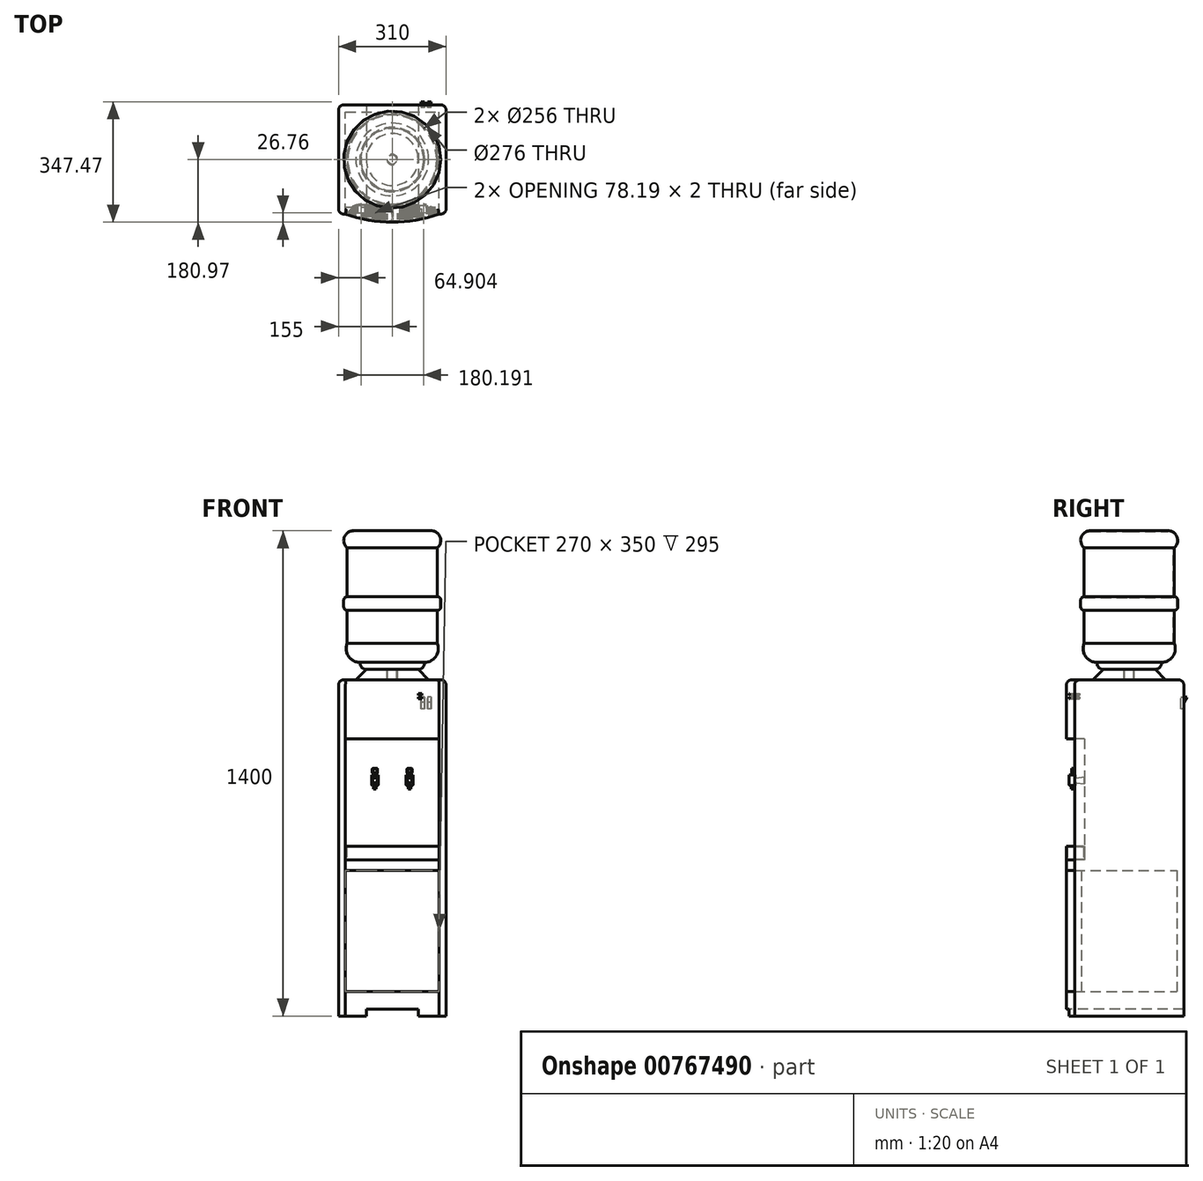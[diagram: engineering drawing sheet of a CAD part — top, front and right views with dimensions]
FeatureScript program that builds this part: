
annotation { "Feature Type Name" : "Feature", "Feature Type Description" : "" }
export const myFeature = defineFeature(function(context is Context, id is Id, definition is map)
    precondition{}
    {
        {
            var Q0;
            Q0=qCreatedBy(makeId("Top.planeOp"),FACE);
            var sketch = newSketch(context, id + "F0", { "sketchPlane" : qUnion([Q0])});
            skLineSegment(sketch, "E0.bottom", {"start": v(155, -157.5) * mm, "end": v(-155, -157.5) * mm});
            skLineSegment(sketch, "E0.top", {"start": v(155, 157.5) * mm, "end": v(-155, 157.5) * mm});
            skLineSegment(sketch, "E0.left", {"start": v(155, -157.5) * mm, "end": v(155, 157.5) * mm});
            skLineSegment(sketch, "E0.right", {"start": v(-155, -157.5) * mm, "end": v(-155, 157.5) * mm});
            skPoint(sketch, "E0.middle", {"position": v(0, 0) * mm});
            skArc(sketch, "E1", {"start": v(-135, -157.5) * mm, "mid": v(0, -180.97) * mm, "end": v(135, -157.5) * mm});
            skSolve(sketch);
        }
        {
            var Q0;
            Q0=makeQuery(id+"F0.imprint","IMPRINT",FACE,{"disambiguationData":[TD([[makeQuery(id+"F0.imprint","IMPRINT",EDGE,{"derivedFrom":sQuery(id+"F0.wireOp",EDGE,"E0.bottom")}),-1.0]])]});
            var Q1;
            {var subQ0=sQuery(id+"F0.wireOp",EDGE,"E1");Q1=makeQuery(id+"F0.imprint","IMPRINT",FACE,{"disambiguationData":[TD([[makeQuery(id+"F0.imprint","IMPRINT",EDGE,{"derivedFrom":subQ0}),1.0]])]});}
            extrude(context, id + "F1", {"entities" : qUnion([Q0, Q1]), "depth" : 970 * mm, "offsetDistance" : 25 * mm});
        }
        {
            var Q0;
            Q0=qCreatedBy(makeId("Front.planeOp"),FACE);
            var sketch = newSketch(context, id + "F2", { "sketchPlane" : qUnion([Q0])});
            skLineSegment(sketch, "E2.0", {"start": v(155, 970) * mm, "end": v(-155, 970) * mm});
            skLineSegment(sketch, "E3", {"start": v(105, 970) * mm, "end": v(75, 1000) * mm});
            skLineSegment(sketch, "E4", {"start": v(75, 1000) * mm, "end": v(0, 1000) * mm});
            skLineSegment(sketch, "E5", {"start": v(0, 1000) * mm, "end": v(0, 970) * mm});
            skLineSegment(sketch, "E6", {"start": v(15, 1000) * mm, "end": v(15, 970) * mm});
            skSolve(sketch);
        }
        {
            var Q0;
            {var subQ0=sQuery(id+"F2.wireOp",EDGE,"E3");Q0=makeQuery(id+"F2.imprint","IMPRINT",FACE,{"disambiguationData":[TD([[makeQuery(id+"F2.imprint","IMPRINT",EDGE,{"derivedFrom":subQ0}),1.0]])]});}
            var Q1;
            Q1=sQuery(id+"F2.wireOp",EDGE,"E5");
            revolve(context, id + "F3", {"operationType" : NewBodyOperationType.ADD, "surfaceOperationType" : NewSurfaceOperationType.NEW, "entities" : qUnion([Q0]), "axis" : qUnion([Q1]), "revolveType" : RevolveType.FULL});
        }
        {
            var Q0;
            Q0=qCreatedBy(makeId("Top.planeOp"),FACE);
            cPlane(context, id + "F4", {"entities" : qUnion([Q0]), "cplaneType" : CPlaneType.OFFSET, "offset" : 450 * mm, "width" : 150 * mm, "height" : 150 * mm});
        }
        {
            var Q0;
            Q0=qCreatedBy(id+"F4.planeOp",FACE);
            var sketch = newSketch(context, id + "F5", { "sketchPlane" : qUnion([Q0])});
            skArc(sketch, "E7.0.0", {"start": v(-135, -157.5) * mm, "mid": v(0, -180.97) * mm, "end": v(135, -157.5) * mm});
            skArc(sketch, "E7.0.2", {"start": v(135, -157.5) * mm, "mid": v(0, -180.97) * mm, "end": v(-135, -157.5) * mm});
            skLineSegment(sketch, "E8", {"start": v(-90, -129.3) * mm, "end": v(0, -129.3) * mm});
            skArc(sketch, "E9", {"start": v(-90, -129.3) * mm, "mid": v(-116.55, -136.93) * mm, "end": v(-135, -157.5) * mm});
            skLineSegment(sketch, "E10.MirrorCS", {"start": v(90, -129.3) * mm, "end": v(0, -129.3) * mm});
            skArc(sketch, "E11.MirrorCS", {"start": v(90, -129.3) * mm, "mid": v(116.55, -136.93) * mm, "end": v(135, -157.5) * mm});
            skSolve(sketch);
        }
        {
            var Q0;
            Q0=qSketchRegion(id+"F5",true);
            extrude(context, id + "F6", {"entities" : qUnion([Q0]), "operationType" : NewBodyOperationType.REMOVE, "depth" : 350 * mm, "offsetDistance" : 25 * mm});
        }
        {
            var Q0;
            Q0=qCreatedBy(makeId("Front.planeOp"),FACE);
            var sketch = newSketch(context, id + "F7", { "sketchPlane" : qUnion([Q0])});
            skLineSegment(sketch, "E12.0", {"start": v(-135, 450) * mm, "end": v(-135, 0) * mm});
            skLineSegment(sketch, "E12.1", {"start": v(135, 450) * mm, "end": v(135, 0) * mm});
            skLineSegment(sketch, "E13", {"start": v(-135, 420) * mm, "end": v(135, 420) * mm});
            skLineSegment(sketch, "E14", {"start": v(-135, 70) * mm, "end": v(135, 70) * mm});
            skSolve(sketch);
        }
        {
            var Q0;
            Q0=qSketchRegion(id+"F7",true);
            extrude(context, id + "F8", {"entities" : qUnion([Q0]), "operationType" : NewBodyOperationType.REMOVE, "endBound" : BoundingType.THROUGH_ALL, "depth" : 25 * mm, "offsetDistance" : 25 * mm, "hasSecondDirection" : true, "secondDirectionOppositeDirection" : true, "secondDirectionDepth" : (315 / 2 - 20) * mm});
        }
        {
            var Q0;
            Q0=qCreatedBy(makeId("Front.planeOp"),FACE);
            var sketch = newSketch(context, id + "F9", { "sketchPlane" : qUnion([Q0])});
            skLineSegment(sketch, "E15.bottom", {"start": v(-75, 20) * mm, "end": v(75, 20) * mm});
            skLineSegment(sketch, "E15.top", {"start": v(-75, 0) * mm, "end": v(75, 0) * mm});
            skLineSegment(sketch, "E15.left", {"start": v(-75, 20) * mm, "end": v(-75, 0) * mm});
            skLineSegment(sketch, "E15.right", {"start": v(75, 20) * mm, "end": v(75, 0) * mm});
            skSolve(sketch);
        }
        {
            var Q0;
            Q0=qSketchRegion(id+"F9",true);
            extrude(context, id + "F10", {"entities" : qUnion([Q0]), "operationType" : NewBodyOperationType.REMOVE, "endBound" : BoundingType.THROUGH_ALL, "oppositeDirection" : true, "depth" : 25 * mm, "offsetDistance" : 25 * mm, "hasSecondDirection" : true, "secondDirectionBound" : SecondDirectionBoundingType.THROUGH_ALL, "secondDirectionOppositeDirection" : false, "secondDirectionDepth" : 25 * mm});
        }
        {
            var Q0;
            Q0=qCreatedBy(makeId("Front.planeOp"),FACE);
            var sketch = newSketch(context, id + "F11", { "sketchPlane" : qUnion([Q0])});
            skLineSegment(sketch, "E16.0", {"start": v(-15, 1000) * mm, "end": v(15, 1000) * mm});
            skLineSegment(sketch, "E17.0.0", {"start": v(-15, 970) * mm, "end": v(15, 970) * mm});
            skLineSegment(sketch, "E18", {"start": v(-15, 970) * mm, "end": v(-15, 1000) * mm});
            skLineSegment(sketch, "E19", {"start": v(0, 1400) * mm, "end": v(-112, 1400) * mm});
            skLineSegment(sketch, "E20", {"start": v(-130, 1350.55) * mm, "end": v(-130, 1210) * mm});
            skLineSegment(sketch, "E21", {"start": v(-130, 1170) * mm, "end": v(-130, 1075) * mm});
            skLineSegment(sketch, "E22.0", {"start": v(-75, 1000) * mm, "end": v(75, 1000) * mm});
            skArc(sketch, "E23", {"start": v(-92.88, 1020.1) * mm, "mid": v(-88.45, 1006.04) * mm, "end": v(-75, 1000) * mm});
            skLineSegment(sketch, "E24", {"start": v(-140, 1200) * mm, "end": v(-140, 1180) * mm});
            skArc(sketch, "E25", {"start": v(-140, 1180) * mm, "mid": v(-137.07, 1172.93) * mm, "end": v(-130, 1170) * mm});
            skLineSegment(sketch, "E26", {"start": v(-140, 1180) * mm, "end": v(-130, 1180) * mm, "construction": true});
            skLineSegment(sketch, "E27", {"start": v(-130, 1170) * mm, "end": v(-130, 1180) * mm, "construction": true});
            skArc(sketch, "E28", {"start": v(-112, 1400) * mm, "mid": v(-138.31, 1381.58) * mm, "end": v(-130, 1350.55) * mm});
            skArc(sketch, "E29", {"start": v(-130, 1210) * mm, "mid": v(-137.07, 1207.07) * mm, "end": v(-140, 1200) * mm});
            skLineSegment(sketch, "E30", {"start": v(-140, 1200) * mm, "end": v(-130, 1200) * mm, "construction": true});
            skLineSegment(sketch, "E31", {"start": v(-130, 1210) * mm, "end": v(-130, 1200) * mm, "construction": true});
            skArc(sketch, "E32", {"start": v(-130, 1075) * mm, "mid": v(-126.01, 1037.7) * mm, "end": v(-92.88, 1020.1) * mm});
            skLineSegment(sketch, "E33", {"start": v(-92.88, 1020.1) * mm, "end": v(0, 1020.1) * mm});
            skLineSegment(sketch, "E34", {"start": v(0, 1400) * mm, "end": v(0, 970) * mm});
            skLineSegment(sketch, "E35.0", {"start": v(-75, 1002) * mm, "end": v(75, 1002) * mm});
            skArc(sketch, "E35.1", {"start": v(-90.44, 1022.18) * mm, "mid": v(-87.7, 1008.28) * mm, "end": v(-75, 1002) * mm});
            skArc(sketch, "E35.2", {"start": v(-128, 1074.6) * mm, "mid": v(-123.77, 1037.98) * mm, "end": v(-90.44, 1022.18) * mm});
            skLineSegment(sketch, "E35.3", {"start": v(-128, 1172.25) * mm, "end": v(-128, 1074.6) * mm});
            skArc(sketch, "E35.4", {"start": v(-138, 1180) * mm, "mid": v(-134.9, 1173.68) * mm, "end": v(-128, 1172.25) * mm});
            skLineSegment(sketch, "E35.5", {"start": v(-138, 1200) * mm, "end": v(-138, 1180) * mm});
            skLineSegment(sketch, "E35.6", {"start": v(0, 1398) * mm, "end": v(-112, 1398) * mm});
            skArc(sketch, "E35.7", {"start": v(-112, 1398) * mm, "mid": v(-136.58, 1380.46) * mm, "end": v(-128, 1351.5) * mm});
            skLineSegment(sketch, "E35.8", {"start": v(-128, 1351.5) * mm, "end": v(-128, 1207.75) * mm});
            skArc(sketch, "E35.9", {"start": v(-128, 1207.75) * mm, "mid": v(-134.9, 1206.32) * mm, "end": v(-138, 1200) * mm});
            skLineSegment(sketch, "E36", {"start": v(-13, 970) * mm, "end": v(-13, 1002) * mm});
            skSolve(sketch);
        }
        {
            var Q0;
            {var subQ3=sQuery(id+"F11.wireOp",EDGE,"E18");Q0=makeQuery(id+"F11.imprint","IMPRINT",FACE,{"disambiguationData":[TD([[makeQuery(id+"F11.imprint","IMPRINT",EDGE,{"derivedFrom":subQ3}),-1.0]])]});}
            var Q1;
            {var subQ0=sQuery(id+"F11.wireOp",EDGE,"E23");Q1=makeQuery(id+"F11.imprint","IMPRINT",FACE,{"disambiguationData":[TD([[makeQuery(id+"F11.imprint","IMPRINT",EDGE,{"derivedFrom":subQ0}),1.0]])]});}
            var Q2;
            {var subQ4=sQuery(id+"F11.wireOp",EDGE,"E19");Q2=makeQuery(id+"F11.imprint","IMPRINT",FACE,{"disambiguationData":[TD([[makeQuery(id+"F11.imprint","IMPRINT",EDGE,{"derivedFrom":subQ4}),1.0]])]});}
            var Q3;
            Q3=sQuery(id+"F11.wireOp",EDGE,"E34");
            revolve(context, id + "F12", {"surfaceOperationType" : NewSurfaceOperationType.NEW, "entities" : qUnion([Q0, Q1, Q2]), "axis" : qUnion([Q3]), "revolveType" : RevolveType.FULL});
        }
        {
            var Q0;
            Q0=makeQuery(id+"F1.opExtrude","SWEPT_EDGE",EDGE,{"disambiguationData":[OSD([sQuery(id+"F0.wireOp",EDGE,"E0.top"),sQuery(id+"F0.wireOp",EDGE,"E0.right")])]});
            var Q1;
            Q1=makeQuery(id+"F1.opExtrude","SWEPT_EDGE",EDGE,{"disambiguationData":[OSD([sQuery(id+"F0.wireOp",EDGE,"E0.bottom"),sQuery(id+"F0.wireOp",EDGE,"E0.right")])]});
            var Q2;
            Q2=makeQuery(id+"F1.opExtrude","SWEPT_EDGE",EDGE,{"disambiguationData":[OSD([sQuery(id+"F0.wireOp",EDGE,"E0.bottom"),sQuery(id+"F0.wireOp",EDGE,"E0.left")])]});
            var Q3;
            Q3=makeQuery(id+"F1.opExtrude","SWEPT_EDGE",EDGE,{"disambiguationData":[OSD([sQuery(id+"F0.wireOp",EDGE,"E0.top"),sQuery(id+"F0.wireOp",EDGE,"E0.left")])]});
            var Q4;
            Q4=makeQuery(id+"F1.opExtrude","CAP_EDGE",EDGE,{"disambiguationData":[OSD([sQuery(id+"F0.wireOp",EDGE,"E0.top")])],"isStart":false});
            var Q5;
            Q5=makeQuery(id+"F1.opExtrude","CAP_EDGE",EDGE,{"disambiguationData":[OSD([sQuery(id+"F0.wireOp",EDGE,"E0.left")])],"isStart":false});
            var Q6;
            Q6=makeQuery(id+"F1.opExtrude","CAP_EDGE",EDGE,{"disambiguationData":[OSD([sQuery(id+"F0.wireOp",EDGE,"E0.right")])],"isStart":false});
            var Q7;
            Q7=makeQuery(id+"F1.opExtrude","CAP_EDGE",EDGE,{"disambiguationData":[OSD([sQuery(id+"F0.wireOp",EDGE,"E1")])],"isStart":false});
            var Q8;
            {var subQ0=sQuery(id+"F0.wireOp",EDGE,"E0.bottom");Q8=makeQuery(id+"F1.opExtrude","CAP_EDGE",EDGE,{"disambiguationData":[OSD([subQ0]),TDD([makeQuery(id+"F0.imprint","IMPRINT",EDGE,{"disambiguationData":[TD([[makeQuery(id+"F0.imprint","INTERSECT",VERTEX,{"derivedFrom":[subQ0,sQuery(id+"F0.wireOp",EDGE,"E0.right")]}),1.0]])],"derivedFrom":subQ0})])],"isStart":false});}
            var Q9;
            {var subQ0=sQuery(id+"F0.wireOp",EDGE,"E0.bottom");Q9=makeQuery(id+"F1.opExtrude","CAP_EDGE",EDGE,{"disambiguationData":[OSD([subQ0]),TDD([makeQuery(id+"F0.imprint","IMPRINT",EDGE,{"disambiguationData":[TD([[makeQuery(id+"F0.imprint","INTERSECT",VERTEX,{"derivedFrom":[subQ0,sQuery(id+"F0.wireOp",EDGE,"E0.left")]}),-1.0]])],"derivedFrom":subQ0})])],"isStart":false});}
            fillet(context, id + "F13", {"entities" : qUnion([Q0, Q1, Q2, Q3, Q4, Q5, Q6, Q7, Q8, Q9]), "radius" : 15 * mm, "tangentPropagation" : true, "allowEdgeOverflow" : false});
        }
        {
            var Q0;
            Q0=makeQuery(id+"F6.boolean.opBoolean","COPY",FACE,{"derivedFrom":makeQuery(id+"F6.opExtrude","CAP_FACE",FACE,{"disambiguationData":[OSD([sQuery(id+"F5.wireOp",EDGE,"E7.0.2"),sQuery(id+"F5.wireOp",EDGE,"E8"),sQuery(id+"F5.wireOp",EDGE,"E9"),sQuery(id+"F5.wireOp",EDGE,"E10.MirrorCS"),sQuery(id+"F5.wireOp",EDGE,"E11.MirrorCS")])],"isStart":true})});
            var sketch = newSketch(context, id + "F14", { "sketchPlane" : qUnion([Q0])});
            skArc(sketch, "E37.0", {"start": v(-90, -129.3) * mm, "mid": v(-116.55, -136.93) * mm, "end": v(-135, -157.5) * mm});
            skLineSegment(sketch, "E37.1", {"start": v(90, -129.3) * mm, "end": v(-90, -129.3) * mm});
            skArc(sketch, "E37.2", {"start": v(90, -129.3) * mm, "mid": v(116.55, -136.93) * mm, "end": v(135, -157.5) * mm});
            skArc(sketch, "E37.3", {"start": v(135, -157.5) * mm, "mid": v(0, -180.97) * mm, "end": v(-135, -157.5) * mm});
            skSolve(sketch);
        }
        {
            var Q0;
            Q0=makeQuery(id+"F14.imprint","IMPRINT",FACE,{"disambiguationData":[TD([[makeQuery(id+"F14.imprint","IMPRINT",EDGE,{"derivedFrom":sQuery(id+"F14.wireOp",EDGE,"E37.0")}),1.0]])]});
            var Q1;
            Q1=qConstructionFilter(qBodyType(qCreatedBy(id+"F14",EDGE),BodyType.WIRE),ConstructionObject.NO);
            extrude(context, id + "F15", {"entities" : qUnion([Q0]), "surfaceEntities" : qUnion([Q1]), "depth" : 40 * mm, "offsetDistance" : 25 * mm});
        }
        {
            var Q0;
            Q0=makeQuery(id+"F15.opExtrude","CAP_FACE",FACE,{"disambiguationData":[OSD([sQuery(id+"F14.wireOp",EDGE,"E37.0"),sQuery(id+"F14.wireOp",EDGE,"E37.1"),sQuery(id+"F14.wireOp",EDGE,"E37.2"),sQuery(id+"F14.wireOp",EDGE,"E37.3")])],"isStart":false});
            shell(context, id + "F16", {"entities" : qUnion([Q0]), "thickness" : 2 * mm});
        }
        {
            var Q0;
            Q0=makeQuery(id+"F15.opExtrude","CAP_FACE",FACE,{"disambiguationData":[OSD([sQuery(id+"F14.wireOp",EDGE,"E37.0"),sQuery(id+"F14.wireOp",EDGE,"E37.1"),sQuery(id+"F14.wireOp",EDGE,"E37.2"),sQuery(id+"F14.wireOp",EDGE,"E37.3")])],"isStart":false});
            var sketch = newSketch(context, id + "F17", { "sketchPlane" : qUnion([Q0])});
            skArc(sketch, "E38.0", {"start": v(-90, -131.3) * mm, "mid": v(-114.54, -138.04) * mm, "end": v(-132.18, -156.38) * mm});
            skLineSegment(sketch, "E38.1", {"start": v(90, -131.3) * mm, "end": v(-90, -131.3) * mm});
            skArc(sketch, "E38.2", {"start": v(132.18, -156.38) * mm, "mid": v(0, -178.97) * mm, "end": v(-132.18, -156.38) * mm});
            skArc(sketch, "E38.3", {"start": v(90, -131.3) * mm, "mid": v(114.54, -138.04) * mm, "end": v(132.18, -156.38) * mm});
            skLineSegment(sketch, "E39.0", {"start": v(90, -133.3) * mm, "end": v(-90, -133.3) * mm});
            skArc(sketch, "E39.1", {"start": v(90, -133.3) * mm, "mid": v(112.5, -139.17) * mm, "end": v(129.24, -155.29) * mm});
            skArc(sketch, "E39.2", {"start": v(129.24, -155.29) * mm, "mid": v(0, -176.97) * mm, "end": v(-129.24, -155.29) * mm});
            skArc(sketch, "E39.3", {"start": v(-90, -133.3) * mm, "mid": v(-112.5, -139.17) * mm, "end": v(-129.24, -155.29) * mm});
            skLineSegment(sketch, "E40", {"start": v(0, -112.71) * mm, "end": v(0, -215.15) * mm, "construction": true});
            skLineSegment(sketch, "E41", {"start": v(-50, -106.6) * mm, "end": v(-50, -205.9) * mm, "construction": true});
            skLineSegment(sketch, "E42.bottom", {"start": v(-57.5, -156.3) * mm, "end": v(-42.5, -156.3) * mm});
            skLineSegment(sketch, "E42.top", {"start": v(-57.5, -171.3) * mm, "end": v(-42.5, -171.3) * mm});
            skLineSegment(sketch, "E42.left", {"start": v(-57.5, -156.3) * mm, "end": v(-57.5, -171.3) * mm});
            skLineSegment(sketch, "E42.right", {"start": v(-42.5, -156.3) * mm, "end": v(-42.5, -171.3) * mm});
            skLineSegment(sketch, "E43", {"start": v(-51, -156.3) * mm, "end": v(-51, -133.3) * mm});
            skLineSegment(sketch, "E44.MirrorCS", {"start": v(-49, -156.3) * mm, "end": v(-49, -133.3) * mm});
            skLineSegment(sketch, "E45", {"start": v(-51, -171.3) * mm, "end": v(-51, -173.67) * mm});
            skLineSegment(sketch, "E46", {"start": v(-49, -171.3) * mm, "end": v(-49, -173.93) * mm});
            skLineSegment(sketch, "E47", {"start": v(-1, -133.3) * mm, "end": v(-1, -176.97) * mm});
            skLineSegment(sketch, "E48", {"start": v(1, -133.3) * mm, "end": v(1, -176.97) * mm});
            skLineSegment(sketch, "E49", {"start": v(-49, -135.21) * mm, "end": v(-1, -135.21) * mm});
            skLineSegment(sketch, "E50.0.1.0", {"start": v(-49, -137.21) * mm, "end": v(-1, -137.21) * mm});
            skLineSegment(sketch, "E50.0.2.0", {"start": v(-49, -139.21) * mm, "end": v(-1, -139.21) * mm});
            skLineSegment(sketch, "E50.0.3.0", {"start": v(-49, -141.21) * mm, "end": v(-1, -141.21) * mm});
            skLineSegment(sketch, "E50.0.4.0", {"start": v(-49, -143.21) * mm, "end": v(-1, -143.21) * mm});
            skLineSegment(sketch, "E50.0.5.0", {"start": v(-49, -145.21) * mm, "end": v(-1, -145.21) * mm});
            skLineSegment(sketch, "E50.0.6.0", {"start": v(-49, -147.21) * mm, "end": v(-1, -147.21) * mm});
            skLineSegment(sketch, "E50.0.7.0", {"start": v(-49, -149.21) * mm, "end": v(-1, -149.21) * mm});
            skLineSegment(sketch, "E50.0.8.0", {"start": v(-49, -151.21) * mm, "end": v(-1, -151.21) * mm});
            skLineSegment(sketch, "E50.0.9.0", {"start": v(-49, -153.21) * mm, "end": v(-1, -153.21) * mm});
            skLineSegment(sketch, "E50.0.10.0", {"start": v(-49, -155.21) * mm, "end": v(-1, -155.21) * mm});
            skLineSegment(sketch, "E50.0.11.0", {"start": v(-42.5, -157.21) * mm, "end": v(-1, -157.21) * mm});
            skLineSegment(sketch, "E50.0.12.0", {"start": v(-44.5, -159.21) * mm, "end": v(-1, -159.21) * mm});
            skLineSegment(sketch, "E50.0.13.0", {"start": v(-44.5, -161.21) * mm, "end": v(-1, -161.21) * mm});
            skLineSegment(sketch, "E50.0.14.0", {"start": v(-44.5, -163.21) * mm, "end": v(-1, -163.21) * mm});
            skLineSegment(sketch, "E50.0.15.0", {"start": v(-49, -165.21) * mm, "end": v(-1, -165.21) * mm});
            skLineSegment(sketch, "E50.0.16.0", {"start": v(-49, -167.21) * mm, "end": v(-1, -167.21) * mm});
            skLineSegment(sketch, "E50.0.17.0", {"start": v(-49, -169.21) * mm, "end": v(-1, -169.21) * mm});
            skLineSegment(sketch, "E50.0.18.0", {"start": v(-49, -171.21) * mm, "end": v(-1, -171.21) * mm});
            skLineSegment(sketch, "E50.0.19.0", {"start": v(-49, -173.21) * mm, "end": v(-1, -173.21) * mm});
            skLineSegment(sketch, "E50.0.20.0", {"start": v(-49, -175.21) * mm, "end": v(-1, -175.21) * mm});
            skLineSegment(sketch, "E50.direction1", {"start": v(-49, -135.21) * mm, "end": v(-24, -135.21) * mm, "construction": true});
            skLineSegment(sketch, "E50.direction2", {"start": v(-49, -135.21) * mm, "end": v(-49, -137.21) * mm, "construction": true});
            skLineSegment(sketch, "E51.MirrorCS", {"start": v(-51, -137.21) * mm, "end": v(-108.57, -137.21) * mm});
            skLineSegment(sketch, "E52.MirrorCS", {"start": v(-51, -139.21) * mm, "end": v(-112.57, -139.21) * mm});
            skLineSegment(sketch, "E53.MirrorCS", {"start": v(-51, -141.21) * mm, "end": v(-115.8, -141.21) * mm});
            skLineSegment(sketch, "E54.MirrorCS", {"start": v(-51, -143.21) * mm, "end": v(-118.53, -143.21) * mm});
            skLineSegment(sketch, "E55.MirrorCS", {"start": v(-51, -145.21) * mm, "end": v(-120.9, -145.21) * mm});
            skLineSegment(sketch, "E56.MirrorCS", {"start": v(-51, -147.21) * mm, "end": v(-122.96, -147.21) * mm});
            skLineSegment(sketch, "E57.MirrorCS", {"start": v(-51, -149.21) * mm, "end": v(-124.8, -149.21) * mm});
            skLineSegment(sketch, "E58.MirrorCS", {"start": v(-51, -151.21) * mm, "end": v(-126.43, -151.21) * mm});
            skLineSegment(sketch, "E59.MirrorCS", {"start": v(-51, -153.21) * mm, "end": v(-127.89, -153.21) * mm});
            skLineSegment(sketch, "E60.MirrorCS", {"start": v(-51, -155.21) * mm, "end": v(-129.2, -155.21) * mm});
            skLineSegment(sketch, "E61.MirrorCS", {"start": v(-57.5, -157.21) * mm, "end": v(-123.53, -157.21) * mm});
            skLineSegment(sketch, "E62.MirrorCS", {"start": v(-57.5, -159.21) * mm, "end": v(-117.26, -159.21) * mm});
            skLineSegment(sketch, "E63.MirrorCS", {"start": v(-57.5, -161.21) * mm, "end": v(-110.6, -161.21) * mm});
            skLineSegment(sketch, "E64.MirrorCS", {"start": v(-57.5, -163.21) * mm, "end": v(-103.48, -163.21) * mm});
            skLineSegment(sketch, "E65.MirrorCS", {"start": v(-49, -165.21) * mm, "end": v(-50, -165.21) * mm});
            skLineSegment(sketch, "E66.MirrorCS", {"start": v(-57.5, -167.21) * mm, "end": v(-99, -167.21) * mm});
            skLineSegment(sketch, "E67.MirrorCS", {"start": v(-57.5, -169.21) * mm, "end": v(-99, -169.21) * mm});
            skLineSegment(sketch, "E68.MirrorCS", {"start": v(-51, -171.21) * mm, "end": v(-99, -171.21) * mm});
            skLineSegment(sketch, "E69.MirrorCS", {"start": v(-51, -173.21) * mm, "end": v(-99, -173.21) * mm});
            skPoint(sketch, "E70.orphan", {"position": v(-99, -137.21) * mm});
            skPoint(sketch, "E71.orphan", {"position": v(-99, -139.21) * mm});
            skPoint(sketch, "E72.orphan", {"position": v(-99, -141.21) * mm});
            skPoint(sketch, "E73.orphan", {"position": v(-99, -143.21) * mm});
            skPoint(sketch, "E74.orphan", {"position": v(-99, -145.21) * mm});
            skPoint(sketch, "E75.orphan", {"position": v(-99, -147.21) * mm});
            skPoint(sketch, "E76.orphan", {"position": v(-99, -149.21) * mm});
            skPoint(sketch, "E77.orphan", {"position": v(-99, -151.21) * mm});
            skPoint(sketch, "E78.orphan", {"position": v(-99, -153.21) * mm});
            skPoint(sketch, "E79.orphan", {"position": v(-99, -155.21) * mm});
            skPoint(sketch, "E80.orphan", {"position": v(-99, -157.21) * mm});
            skPoint(sketch, "E81.orphan", {"position": v(-99, -159.21) * mm});
            skPoint(sketch, "E82.orphan", {"position": v(-99, -161.21) * mm});
            skPoint(sketch, "E83.orphan", {"position": v(-99, -163.21) * mm});
            skLineSegment(sketch, "E84", {"start": v(-51, -135.21) * mm, "end": v(-103.14, -135.21) * mm});
            skLineSegment(sketch, "E85.0", {"start": v(-55.5, -158.3) * mm, "end": v(-44.5, -158.3) * mm});
            skLineSegment(sketch, "E85.1", {"start": v(-55.5, -158.3) * mm, "end": v(-55.5, -169.3) * mm});
            skLineSegment(sketch, "E85.2", {"start": v(-55.5, -169.3) * mm, "end": v(-44.5, -169.3) * mm});
            skLineSegment(sketch, "E85.3", {"start": v(-44.5, -158.3) * mm, "end": v(-44.5, -169.3) * mm});
            skPoint(sketch, "E86.orphan", {"position": v(-51, -157.21) * mm});
            skPoint(sketch, "E87.orphan", {"position": v(-51, -161.21) * mm});
            skPoint(sketch, "E88.orphan", {"position": v(-51, -165.21) * mm});
            skPoint(sketch, "E89.orphan", {"position": v(-51, -159.21) * mm});
            skPoint(sketch, "E90.orphan", {"position": v(-51, -163.21) * mm});
            skLineSegment(sketch, "E91.trimOffspring", {"start": v(-57.5, -165.21) * mm, "end": v(-99, -165.21) * mm});
            skPoint(sketch, "E92.orphan", {"position": v(-51, -167.21) * mm});
            skPoint(sketch, "E93.orphan", {"position": v(-51, -169.21) * mm});
            skPoint(sketch, "E94.orphan", {"position": v(-49, -159.21) * mm});
            skPoint(sketch, "E95.orphan", {"position": v(-49, -157.21) * mm});
            skPoint(sketch, "E96.orphan", {"position": v(-49, -161.21) * mm});
            skPoint(sketch, "E97.orphan", {"position": v(-49, -163.21) * mm});
            skLineSegment(sketch, "E98.MirrorCS", {"start": v(49, -165.21) * mm, "end": v(1, -165.21) * mm});
            skLineSegment(sketch, "E99.MirrorCS", {"start": v(44.5, -163.21) * mm, "end": v(1, -163.21) * mm});
            skLineSegment(sketch, "E100.MirrorCS", {"start": v(49, -167.21) * mm, "end": v(1, -167.21) * mm});
            skLineSegment(sketch, "E101.MirrorCS", {"start": v(44.5, -159.21) * mm, "end": v(1, -159.21) * mm});
            skLineSegment(sketch, "E102.MirrorCS", {"start": v(49, -171.21) * mm, "end": v(1, -171.21) * mm});
            skLineSegment(sketch, "E103.MirrorCS", {"start": v(42.5, -157.21) * mm, "end": v(1, -157.21) * mm});
            skLineSegment(sketch, "E104.MirrorCS", {"start": v(49, -175.21) * mm, "end": v(1, -175.21) * mm});
            skLineSegment(sketch, "E105.MirrorCS", {"start": v(49, -173.21) * mm, "end": v(1, -173.21) * mm});
            skLineSegment(sketch, "E106.MirrorCS", {"start": v(44.5, -161.21) * mm, "end": v(1, -161.21) * mm});
            skLineSegment(sketch, "E107.MirrorCS", {"start": v(49, -169.21) * mm, "end": v(1, -169.21) * mm});
            skLineSegment(sketch, "E108.MirrorCS", {"start": v(49, -135.21) * mm, "end": v(1, -135.21) * mm});
            skLineSegment(sketch, "E109.MirrorCS", {"start": v(49, -145.21) * mm, "end": v(1, -145.21) * mm});
            skLineSegment(sketch, "E110.MirrorCS", {"start": v(49, -137.21) * mm, "end": v(1, -137.21) * mm});
            skLineSegment(sketch, "E111.MirrorCS", {"start": v(49, -143.21) * mm, "end": v(1, -143.21) * mm});
            skLineSegment(sketch, "E112.MirrorCS", {"start": v(49, -153.21) * mm, "end": v(1, -153.21) * mm});
            skLineSegment(sketch, "E113.MirrorCS", {"start": v(49, -141.21) * mm, "end": v(1, -141.21) * mm});
            skLineSegment(sketch, "E114.MirrorCS", {"start": v(49, -151.21) * mm, "end": v(1, -151.21) * mm});
            skLineSegment(sketch, "E115.MirrorCS", {"start": v(49, -149.21) * mm, "end": v(1, -149.21) * mm});
            skLineSegment(sketch, "E116.MirrorCS", {"start": v(49, -147.21) * mm, "end": v(1, -147.21) * mm});
            skLineSegment(sketch, "E117.MirrorCS", {"start": v(49, -139.21) * mm, "end": v(1, -139.21) * mm});
            skLineSegment(sketch, "E118.MirrorCS", {"start": v(49, -155.21) * mm, "end": v(1, -155.21) * mm});
            skLineSegment(sketch, "E119.MirrorCS", {"start": v(42.5, -156.3) * mm, "end": v(42.5, -171.3) * mm});
            skLineSegment(sketch, "E120.MirrorCS", {"start": v(44.5, -158.3) * mm, "end": v(44.5, -169.3) * mm});
            skLineSegment(sketch, "E121.MirrorCS", {"start": v(55.5, -158.3) * mm, "end": v(55.5, -169.3) * mm});
            skLineSegment(sketch, "E122.MirrorCS", {"start": v(57.5, -156.3) * mm, "end": v(42.5, -156.3) * mm});
            skLineSegment(sketch, "E123.MirrorCS", {"start": v(51, -171.21) * mm, "end": v(99, -171.21) * mm});
            skLineSegment(sketch, "E124.MirrorCS", {"start": v(57.5, -156.3) * mm, "end": v(57.5, -171.3) * mm});
            skLineSegment(sketch, "E125.MirrorCS", {"start": v(57.5, -171.3) * mm, "end": v(42.5, -171.3) * mm});
            skLineSegment(sketch, "E126.MirrorCS", {"start": v(49, -171.3) * mm, "end": v(49, -173.93) * mm});
            skLineSegment(sketch, "E127.MirrorCS", {"start": v(51, -171.3) * mm, "end": v(51, -173.67) * mm});
            skLineSegment(sketch, "E128.MirrorCS", {"start": v(51, -151.21) * mm, "end": v(126.43, -151.21) * mm});
            skLineSegment(sketch, "E129.MirrorCS", {"start": v(51, -155.21) * mm, "end": v(129.2, -155.21) * mm});
            skLineSegment(sketch, "E130.MirrorCS", {"start": v(57.5, -165.21) * mm, "end": v(99, -165.21) * mm});
            skLineSegment(sketch, "E131.MirrorCS", {"start": v(57.5, -157.21) * mm, "end": v(123.53, -157.21) * mm});
            skLineSegment(sketch, "E132.MirrorCS", {"start": v(51, -153.21) * mm, "end": v(127.89, -153.21) * mm});
            skLineSegment(sketch, "E133.MirrorCS", {"start": v(57.5, -159.21) * mm, "end": v(117.26, -159.21) * mm});
            skLineSegment(sketch, "E134.MirrorCS", {"start": v(57.5, -167.21) * mm, "end": v(99, -167.21) * mm});
            skLineSegment(sketch, "E135.MirrorCS", {"start": v(51, -141.21) * mm, "end": v(115.8, -141.21) * mm});
            skLineSegment(sketch, "E136.MirrorCS", {"start": v(51, -149.21) * mm, "end": v(124.8, -149.21) * mm});
            skLineSegment(sketch, "E137.MirrorCS", {"start": v(51, -147.21) * mm, "end": v(122.96, -147.21) * mm});
            skLineSegment(sketch, "E138.MirrorCS", {"start": v(51, -137.21) * mm, "end": v(108.57, -137.21) * mm});
            skLineSegment(sketch, "E139.MirrorCS", {"start": v(57.5, -169.21) * mm, "end": v(99, -169.21) * mm});
            skLineSegment(sketch, "E140.MirrorCS", {"start": v(51, -145.21) * mm, "end": v(120.9, -145.21) * mm});
            skLineSegment(sketch, "E141.MirrorCS", {"start": v(51, -139.21) * mm, "end": v(112.57, -139.21) * mm});
            skLineSegment(sketch, "E142.MirrorCS", {"start": v(51, -135.21) * mm, "end": v(103.14, -135.21) * mm});
            skLineSegment(sketch, "E143.MirrorCS", {"start": v(-90, -133.3) * mm, "end": v(90, -133.3) * mm});
            skLineSegment(sketch, "E144.MirrorCS", {"start": v(51, -143.21) * mm, "end": v(118.53, -143.21) * mm});
            skLineSegment(sketch, "E145.MirrorCS", {"start": v(57.5, -163.21) * mm, "end": v(103.48, -163.21) * mm});
            skLineSegment(sketch, "E146.MirrorCS", {"start": v(57.5, -161.21) * mm, "end": v(110.6, -161.21) * mm});
            skPoint(sketch, "E147.MirrorP", {"position": v(99, -145.21) * mm});
            skPoint(sketch, "E148.MirrorP", {"position": v(99, -141.21) * mm});
            skPoint(sketch, "E149.MirrorP", {"position": v(99, -143.21) * mm});
            skPoint(sketch, "E150.MirrorP", {"position": v(99, -139.21) * mm});
            skPoint(sketch, "E151.MirrorP", {"position": v(99, -137.21) * mm});
            skPoint(sketch, "E152.MirrorP", {"position": v(99, -155.21) * mm});
            skPoint(sketch, "E153.MirrorP", {"position": v(99, -147.21) * mm});
            skPoint(sketch, "E154.MirrorP", {"position": v(99, -149.21) * mm});
            skPoint(sketch, "E155.MirrorP", {"position": v(99, -157.21) * mm});
            skPoint(sketch, "E156.MirrorP", {"position": v(99, -151.21) * mm});
            skPoint(sketch, "E157.MirrorP", {"position": v(99, -153.21) * mm});
            skLineSegment(sketch, "E158.MirrorCS", {"start": v(55.5, -158.3) * mm, "end": v(44.5, -158.3) * mm});
            skLineSegment(sketch, "E159.MirrorCS", {"start": v(55.5, -169.3) * mm, "end": v(44.5, -169.3) * mm});
            skLineSegment(sketch, "E160.MirrorCS", {"start": v(51, -156.3) * mm, "end": v(51, -133.3) * mm});
            skLineSegment(sketch, "E161.MirrorCS", {"start": v(49, -156.3) * mm, "end": v(49, -133.3) * mm});
            skLineSegment(sketch, "E162.MirrorCS", {"start": v(51, -173.21) * mm, "end": v(99, -173.21) * mm});
            skSolve(sketch);
        }
        {
            var Q0;
            {var subQ16=sQuery(id+"F17.wireOp",EDGE,"E38.0");Q0=makeQuery(id+"F17.imprint","IMPRINT",FACE,{"disambiguationData":[TD([[makeQuery(id+"F17.imprint","IMPRINT",EDGE,{"derivedFrom":subQ16}),1.0]])]});}
            var Q1;
            {var subQ0=sQuery(id+"F17.wireOp",EDGE,"E66.MirrorCS");var subQ1=sQuery(id+"F17.wireOp",EDGE,"E38.2");var subQ2=makeQuery(id+"F17.imprint","INTERSECT",VERTEX,{"derivedFrom":[subQ1,subQ0]});Q1=makeQuery(id+"F17.imprint","IMPRINT",FACE,{"disambiguationData":[TD([[makeQuery(id+"F17.imprint","IMPRINT",EDGE,{"disambiguationData":[TD([[subQ2,1.0]])],"derivedFrom":subQ1}),-1.0]])]});}
            var Q2;
            {var subQ0=sQuery(id+"F17.wireOp",EDGE,"E67.MirrorCS");var subQ1=sQuery(id+"F17.wireOp",EDGE,"E38.2");var subQ2=makeQuery(id+"F17.imprint","INTERSECT",VERTEX,{"derivedFrom":[subQ1,subQ0]});Q2=makeQuery(id+"F17.imprint","IMPRINT",FACE,{"disambiguationData":[TD([[makeQuery(id+"F17.imprint","IMPRINT",EDGE,{"disambiguationData":[TD([[subQ2,1.0]])],"derivedFrom":subQ1}),-1.0]])]});}
            var Q3;
            {var subQ0=sQuery(id+"F17.wireOp",EDGE,"E68.MirrorCS");var subQ1=sQuery(id+"F17.wireOp",EDGE,"E38.2");var subQ2=makeQuery(id+"F17.imprint","INTERSECT",VERTEX,{"derivedFrom":[subQ1,subQ0]});Q3=makeQuery(id+"F17.imprint","IMPRINT",FACE,{"disambiguationData":[TD([[makeQuery(id+"F17.imprint","IMPRINT",EDGE,{"disambiguationData":[TD([[subQ2,1.0]])],"derivedFrom":subQ1}),-1.0]])]});}
            var Q4;
            {var subQ0=sQuery(id+"F17.wireOp",EDGE,"E134.MirrorCS");var subQ1=sQuery(id+"F17.wireOp",EDGE,"E38.2");var subQ2=makeQuery(id+"F17.imprint","INTERSECT",VERTEX,{"derivedFrom":[subQ1,subQ0]});Q4=makeQuery(id+"F17.imprint","IMPRINT",FACE,{"disambiguationData":[TD([[makeQuery(id+"F17.imprint","IMPRINT",EDGE,{"disambiguationData":[TD([[subQ2,-1.0]])],"derivedFrom":subQ1}),-1.0]])]});}
            var Q5;
            {var subQ0=sQuery(id+"F17.wireOp",EDGE,"E123.MirrorCS");var subQ1=sQuery(id+"F17.wireOp",EDGE,"E38.2");var subQ2=makeQuery(id+"F17.imprint","INTERSECT",VERTEX,{"derivedFrom":[subQ1,subQ0]});Q5=makeQuery(id+"F17.imprint","IMPRINT",FACE,{"disambiguationData":[TD([[makeQuery(id+"F17.imprint","IMPRINT",EDGE,{"disambiguationData":[TD([[subQ2,1.0]])],"derivedFrom":subQ1}),-1.0]])]});}
            var Q6;
            {var subQ7=sQuery(id+"F17.wireOp",EDGE,"E69.MirrorCS");var subQ9=sQuery(id+"F17.wireOp",EDGE,"E38.2");var subQ10=makeQuery(id+"F17.imprint","INTERSECT",VERTEX,{"derivedFrom":[subQ9,subQ7]});Q6=makeQuery(id+"F17.imprint","IMPRINT",FACE,{"disambiguationData":[TD([[makeQuery(id+"F17.imprint","IMPRINT",EDGE,{"disambiguationData":[TD([[subQ10,1.0]])],"derivedFrom":subQ9}),-1.0]])]});}
            var Q7;
            {var subQ0=sQuery(id+"F17.wireOp",EDGE,"E162.MirrorCS");var subQ1=sQuery(id+"F17.wireOp",EDGE,"E38.2");var subQ2=makeQuery(id+"F17.imprint","INTERSECT",VERTEX,{"derivedFrom":[subQ1,subQ0]});Q7=makeQuery(id+"F17.imprint","IMPRINT",FACE,{"disambiguationData":[TD([[makeQuery(id+"F17.imprint","IMPRINT",EDGE,{"disambiguationData":[TD([[subQ2,1.0]])],"derivedFrom":subQ1}),-1.0]])]});}
            extrude(context, id + "F18", {"entities" : qUnion([Q0, Q1, Q2, Q3, Q4, Q5, Q6, Q7]), "oppositeDirection" : true, "depth" : 2 * mm, "offsetDistance" : 25 * mm});
        }
        {
            var Q0;
            {var subQ0=sQuery(id+"F17.wireOp",EDGE,"E47");var subQ7=sQuery(id+"F17.wireOp",EDGE,"E39.2");var subQ8=makeQuery(id+"F17.imprint","INTERSECT",VERTEX,{"derivedFrom":[subQ7,subQ0]});Q0=makeQuery(id+"F17.imprint","IMPRINT",FACE,{"disambiguationData":[TD([[makeQuery(id+"F17.imprint","IMPRINT",EDGE,{"disambiguationData":[TD([[subQ8,1.0]])],"derivedFrom":subQ7}),-1.0]])]});}
            var Q1;
            {var subQ0=sQuery(id+"F17.wireOp",EDGE,"E49");Q1=makeQuery(id+"F17.imprint","IMPRINT",FACE,{"disambiguationData":[TD([[makeQuery(id+"F17.imprint","IMPRINT",EDGE,{"derivedFrom":subQ0}),-1.0]])]});}
            var Q2;
            {var subQ0=sQuery(id+"F17.wireOp",EDGE,"E50.0.2.0");Q2=makeQuery(id+"F17.imprint","IMPRINT",FACE,{"disambiguationData":[TD([[makeQuery(id+"F17.imprint","IMPRINT",EDGE,{"derivedFrom":subQ0}),-1.0]])]});}
            var Q3;
            {var subQ0=sQuery(id+"F17.wireOp",EDGE,"E50.0.4.0");Q3=makeQuery(id+"F17.imprint","IMPRINT",FACE,{"disambiguationData":[TD([[makeQuery(id+"F17.imprint","IMPRINT",EDGE,{"derivedFrom":subQ0}),-1.0]])]});}
            var Q4;
            {var subQ0=sQuery(id+"F17.wireOp",EDGE,"E50.0.6.0");Q4=makeQuery(id+"F17.imprint","IMPRINT",FACE,{"disambiguationData":[TD([[makeQuery(id+"F17.imprint","IMPRINT",EDGE,{"derivedFrom":subQ0}),-1.0]])]});}
            var Q5;
            {var subQ0=sQuery(id+"F17.wireOp",EDGE,"E50.0.8.0");Q5=makeQuery(id+"F17.imprint","IMPRINT",FACE,{"disambiguationData":[TD([[makeQuery(id+"F17.imprint","IMPRINT",EDGE,{"derivedFrom":subQ0}),-1.0]])]});}
            var Q6;
            {var subQ0=sQuery(id+"F17.wireOp",EDGE,"E50.0.10.0");Q6=makeQuery(id+"F17.imprint","IMPRINT",FACE,{"disambiguationData":[TD([[makeQuery(id+"F17.imprint","IMPRINT",EDGE,{"derivedFrom":subQ0}),-1.0]])]});}
            var Q7;
            {var subQ0=sQuery(id+"F17.wireOp",EDGE,"E50.0.12.0");var subQ1=sQuery(id+"F17.wireOp",EDGE,"E42.right");var subQ2=makeQuery(id+"F17.imprint","INTERSECT",VERTEX,{"derivedFrom":[subQ1,subQ0]});Q7=makeQuery(id+"F17.imprint","IMPRINT",FACE,{"disambiguationData":[TD([[makeQuery(id+"F17.imprint","IMPRINT",EDGE,{"disambiguationData":[TD([[subQ2,-1.0]])],"derivedFrom":subQ1}),1.0]])]});}
            var Q8;
            {var subQ0=sQuery(id+"F17.wireOp",EDGE,"E50.0.14.0");var subQ1=sQuery(id+"F17.wireOp",EDGE,"E42.right");var subQ2=makeQuery(id+"F17.imprint","INTERSECT",VERTEX,{"derivedFrom":[subQ1,subQ0]});Q8=makeQuery(id+"F17.imprint","IMPRINT",FACE,{"disambiguationData":[TD([[makeQuery(id+"F17.imprint","IMPRINT",EDGE,{"disambiguationData":[TD([[subQ2,-1.0]])],"derivedFrom":subQ1}),1.0]])]});}
            var Q9;
            {var subQ0=sQuery(id+"F17.wireOp",EDGE,"E50.0.16.0");var subQ1=sQuery(id+"F17.wireOp",EDGE,"E42.right");var subQ2=makeQuery(id+"F17.imprint","INTERSECT",VERTEX,{"derivedFrom":[subQ1,subQ0]});Q9=makeQuery(id+"F17.imprint","IMPRINT",FACE,{"disambiguationData":[TD([[makeQuery(id+"F17.imprint","IMPRINT",EDGE,{"disambiguationData":[TD([[subQ2,-1.0]])],"derivedFrom":subQ1}),1.0]])]});}
            var Q10;
            {var subQ3=sQuery(id+"F17.wireOp",EDGE,"E50.0.19.0");Q10=makeQuery(id+"F17.imprint","IMPRINT",FACE,{"disambiguationData":[TD([[makeQuery(id+"F17.imprint","IMPRINT",EDGE,{"derivedFrom":subQ3}),1.0]])]});}
            var Q11;
            {var subQ0=sQuery(id+"F17.wireOp",EDGE,"E47");var subQ1=sQuery(id+"F17.wireOp",EDGE,"E39.2");var subQ2=makeQuery(id+"F17.imprint","INTERSECT",VERTEX,{"derivedFrom":[subQ1,subQ0]});Q11=makeQuery(id+"F17.imprint","IMPRINT",FACE,{"disambiguationData":[TD([[makeQuery(id+"F17.imprint","IMPRINT",EDGE,{"disambiguationData":[TD([[subQ2,-1.0]])],"derivedFrom":subQ1}),-1.0]])]});}
            var Q12;
            {var subQ17=sQuery(id+"F17.wireOp",EDGE,"E85.0");Q12=makeQuery(id+"F17.imprint","IMPRINT",FACE,{"disambiguationData":[TD([[makeQuery(id+"F17.imprint","IMPRINT",EDGE,{"derivedFrom":subQ17}),1.0]])]});}
            var Q13;
            {var subQ0=sQuery(id+"F17.wireOp",EDGE,"E50.0.12.0");var subQ1=sQuery(id+"F17.wireOp",EDGE,"E42.right");var subQ2=makeQuery(id+"F17.imprint","INTERSECT",VERTEX,{"derivedFrom":[subQ1,subQ0]});Q13=makeQuery(id+"F17.imprint","IMPRINT",FACE,{"disambiguationData":[TD([[makeQuery(id+"F17.imprint","IMPRINT",EDGE,{"disambiguationData":[TD([[subQ2,-1.0]])],"derivedFrom":subQ1}),-1.0]])]});}
            var Q14;
            {var subQ0=sQuery(id+"F17.wireOp",EDGE,"E50.0.13.0");var subQ1=sQuery(id+"F17.wireOp",EDGE,"E42.right");var subQ2=makeQuery(id+"F17.imprint","INTERSECT",VERTEX,{"derivedFrom":[subQ1,subQ0]});Q14=makeQuery(id+"F17.imprint","IMPRINT",FACE,{"disambiguationData":[TD([[makeQuery(id+"F17.imprint","IMPRINT",EDGE,{"disambiguationData":[TD([[subQ2,-1.0]])],"derivedFrom":subQ1}),-1.0]])]});}
            var Q15;
            {var subQ0=sQuery(id+"F17.wireOp",EDGE,"E50.0.14.0");var subQ1=sQuery(id+"F17.wireOp",EDGE,"E42.right");var subQ2=makeQuery(id+"F17.imprint","INTERSECT",VERTEX,{"derivedFrom":[subQ1,subQ0]});Q15=makeQuery(id+"F17.imprint","IMPRINT",FACE,{"disambiguationData":[TD([[makeQuery(id+"F17.imprint","IMPRINT",EDGE,{"disambiguationData":[TD([[subQ2,-1.0]])],"derivedFrom":subQ1}),-1.0]])]});}
            var Q16;
            {var subQ0=sQuery(id+"F17.wireOp",EDGE,"E50.0.15.0");var subQ1=sQuery(id+"F17.wireOp",EDGE,"E42.right");var subQ2=makeQuery(id+"F17.imprint","INTERSECT",VERTEX,{"derivedFrom":[subQ1,subQ0]});Q16=makeQuery(id+"F17.imprint","IMPRINT",FACE,{"disambiguationData":[TD([[makeQuery(id+"F17.imprint","IMPRINT",EDGE,{"disambiguationData":[TD([[subQ2,-1.0]])],"derivedFrom":subQ1}),-1.0]])]});}
            var Q17;
            {var subQ0=sQuery(id+"F17.wireOp",EDGE,"E50.0.16.0");var subQ1=sQuery(id+"F17.wireOp",EDGE,"E42.right");var subQ2=makeQuery(id+"F17.imprint","INTERSECT",VERTEX,{"derivedFrom":[subQ1,subQ0]});Q17=makeQuery(id+"F17.imprint","IMPRINT",FACE,{"disambiguationData":[TD([[makeQuery(id+"F17.imprint","IMPRINT",EDGE,{"disambiguationData":[TD([[subQ2,-1.0]])],"derivedFrom":subQ1}),-1.0]])]});}
            var Q18;
            {var subQ10=sQuery(id+"F17.wireOp",EDGE,"E42.bottom");var subQ13=sQuery(id+"F17.wireOp",EDGE,"E43");var subQ21=makeQuery(id+"F17.imprint","INTERSECT",VERTEX,{"derivedFrom":[subQ10,subQ13]});Q18=makeQuery(id+"F17.imprint","IMPRINT",FACE,{"disambiguationData":[TD([[makeQuery(id+"F17.imprint","IMPRINT",EDGE,{"disambiguationData":[TD([[subQ21,-1.0]])],"derivedFrom":subQ10}),1.0]])]});}
            var Q19;
            {var subQ0=sQuery(id+"F17.wireOp",EDGE,"E45");var subQ6=sQuery(id+"F17.wireOp",EDGE,"E39.2");var subQ7=makeQuery(id+"F17.imprint","INTERSECT",VERTEX,{"derivedFrom":[subQ6,subQ0]});Q19=makeQuery(id+"F17.imprint","IMPRINT",FACE,{"disambiguationData":[TD([[makeQuery(id+"F17.imprint","IMPRINT",EDGE,{"disambiguationData":[TD([[subQ7,1.0]])],"derivedFrom":subQ6}),-1.0]])]});}
            var Q20;
            {var subQ3=sQuery(id+"F17.wireOp",EDGE,"E69.MirrorCS");var subQ9=sQuery(id+"F17.wireOp",EDGE,"E39.2");var subQ10=makeQuery(id+"F17.imprint","INTERSECT",VERTEX,{"derivedFrom":[subQ9,subQ3]});Q20=makeQuery(id+"F17.imprint","IMPRINT",FACE,{"disambiguationData":[TD([[makeQuery(id+"F17.imprint","IMPRINT",EDGE,{"disambiguationData":[TD([[subQ10,-1.0]])],"derivedFrom":subQ9}),-1.0]])]});}
            var Q21;
            {var subQ0=sQuery(id+"F17.wireOp",EDGE,"E67.MirrorCS");var subQ1=sQuery(id+"F17.wireOp",EDGE,"E39.2");var subQ2=makeQuery(id+"F17.imprint","INTERSECT",VERTEX,{"derivedFrom":[subQ1,subQ0]});Q21=makeQuery(id+"F17.imprint","IMPRINT",FACE,{"disambiguationData":[TD([[makeQuery(id+"F17.imprint","IMPRINT",EDGE,{"disambiguationData":[TD([[subQ2,-1.0]])],"derivedFrom":subQ1}),-1.0]])]});}
            var Q22;
            {var subQ0=sQuery(id+"F17.wireOp",EDGE,"E64.MirrorCS");Q22=makeQuery(id+"F17.imprint","IMPRINT",FACE,{"disambiguationData":[TD([[makeQuery(id+"F17.imprint","IMPRINT",EDGE,{"derivedFrom":subQ0}),1.0]])]});}
            var Q23;
            {var subQ0=sQuery(id+"F17.wireOp",EDGE,"E62.MirrorCS");Q23=makeQuery(id+"F17.imprint","IMPRINT",FACE,{"disambiguationData":[TD([[makeQuery(id+"F17.imprint","IMPRINT",EDGE,{"derivedFrom":subQ0}),1.0]])]});}
            var Q24;
            {var subQ6=sQuery(id+"F17.wireOp",EDGE,"E60.MirrorCS");Q24=makeQuery(id+"F17.imprint","IMPRINT",FACE,{"disambiguationData":[TD([[makeQuery(id+"F17.imprint","IMPRINT",EDGE,{"derivedFrom":subQ6}),1.0]])]});}
            var Q25;
            {var subQ0=sQuery(id+"F17.wireOp",EDGE,"E58.MirrorCS");Q25=makeQuery(id+"F17.imprint","IMPRINT",FACE,{"disambiguationData":[TD([[makeQuery(id+"F17.imprint","IMPRINT",EDGE,{"derivedFrom":subQ0}),1.0]])]});}
            var Q26;
            {var subQ0=sQuery(id+"F17.wireOp",EDGE,"E56.MirrorCS");Q26=makeQuery(id+"F17.imprint","IMPRINT",FACE,{"disambiguationData":[TD([[makeQuery(id+"F17.imprint","IMPRINT",EDGE,{"derivedFrom":subQ0}),1.0]])]});}
            var Q27;
            {var subQ0=sQuery(id+"F17.wireOp",EDGE,"E54.MirrorCS");Q27=makeQuery(id+"F17.imprint","IMPRINT",FACE,{"disambiguationData":[TD([[makeQuery(id+"F17.imprint","IMPRINT",EDGE,{"derivedFrom":subQ0}),1.0]])]});}
            var Q28;
            {var subQ0=sQuery(id+"F17.wireOp",EDGE,"E52.MirrorCS");Q28=makeQuery(id+"F17.imprint","IMPRINT",FACE,{"disambiguationData":[TD([[makeQuery(id+"F17.imprint","IMPRINT",EDGE,{"derivedFrom":subQ0}),1.0]])]});}
            var Q29;
            {var subQ0=sQuery(id+"F17.wireOp",EDGE,"E51.MirrorCS");Q29=makeQuery(id+"F17.imprint","IMPRINT",FACE,{"disambiguationData":[TD([[makeQuery(id+"F17.imprint","IMPRINT",EDGE,{"derivedFrom":subQ0}),-1.0]])]});}
            var Q30;
            {var subQ0=sQuery(id+"F17.wireOp",EDGE,"E108.MirrorCS");Q30=makeQuery(id+"F17.imprint","IMPRINT",FACE,{"disambiguationData":[TD([[makeQuery(id+"F17.imprint","IMPRINT",EDGE,{"derivedFrom":subQ0}),1.0]])]});}
            var Q31;
            {var subQ0=sQuery(id+"F17.wireOp",EDGE,"E113.MirrorCS");Q31=makeQuery(id+"F17.imprint","IMPRINT",FACE,{"disambiguationData":[TD([[makeQuery(id+"F17.imprint","IMPRINT",EDGE,{"derivedFrom":subQ0}),-1.0]])]});}
            var Q32;
            {var subQ0=sQuery(id+"F17.wireOp",EDGE,"E109.MirrorCS");Q32=makeQuery(id+"F17.imprint","IMPRINT",FACE,{"disambiguationData":[TD([[makeQuery(id+"F17.imprint","IMPRINT",EDGE,{"derivedFrom":subQ0}),-1.0]])]});}
            var Q33;
            {var subQ0=sQuery(id+"F17.wireOp",EDGE,"E115.MirrorCS");Q33=makeQuery(id+"F17.imprint","IMPRINT",FACE,{"disambiguationData":[TD([[makeQuery(id+"F17.imprint","IMPRINT",EDGE,{"derivedFrom":subQ0}),-1.0]])]});}
            var Q34;
            {var subQ0=sQuery(id+"F17.wireOp",EDGE,"E112.MirrorCS");Q34=makeQuery(id+"F17.imprint","IMPRINT",FACE,{"disambiguationData":[TD([[makeQuery(id+"F17.imprint","IMPRINT",EDGE,{"derivedFrom":subQ0}),-1.0]])]});}
            var Q35;
            {var subQ1=sQuery(id+"F17.wireOp",EDGE,"E103.MirrorCS");Q35=makeQuery(id+"F17.imprint","IMPRINT",FACE,{"disambiguationData":[TD([[makeQuery(id+"F17.imprint","IMPRINT",EDGE,{"derivedFrom":subQ1}),-1.0]])]});}
            var Q36;
            {var subQ0=sQuery(id+"F17.wireOp",EDGE,"E101.MirrorCS");var subQ1=sQuery(id+"F17.wireOp",EDGE,"E48");var subQ2=makeQuery(id+"F17.imprint","INTERSECT",VERTEX,{"derivedFrom":[subQ1,subQ0]});Q36=makeQuery(id+"F17.imprint","IMPRINT",FACE,{"disambiguationData":[TD([[makeQuery(id+"F17.imprint","IMPRINT",EDGE,{"disambiguationData":[TD([[subQ2,-1.0]])],"derivedFrom":subQ1}),1.0]])]});}
            var Q37;
            {var subQ0=sQuery(id+"F17.wireOp",EDGE,"E98.MirrorCS");var subQ1=sQuery(id+"F17.wireOp",EDGE,"E48");var subQ2=makeQuery(id+"F17.imprint","INTERSECT",VERTEX,{"derivedFrom":[subQ1,subQ0]});Q37=makeQuery(id+"F17.imprint","IMPRINT",FACE,{"disambiguationData":[TD([[makeQuery(id+"F17.imprint","IMPRINT",EDGE,{"disambiguationData":[TD([[subQ2,1.0]])],"derivedFrom":subQ1}),1.0]])]});}
            var Q38;
            {var subQ0=sQuery(id+"F17.wireOp",EDGE,"E100.MirrorCS");var subQ1=sQuery(id+"F17.wireOp",EDGE,"E48");var subQ2=makeQuery(id+"F17.imprint","INTERSECT",VERTEX,{"derivedFrom":[subQ1,subQ0]});Q38=makeQuery(id+"F17.imprint","IMPRINT",FACE,{"disambiguationData":[TD([[makeQuery(id+"F17.imprint","IMPRINT",EDGE,{"disambiguationData":[TD([[subQ2,-1.0]])],"derivedFrom":subQ1}),1.0]])]});}
            var Q39;
            {var subQ5=sQuery(id+"F17.wireOp",EDGE,"E105.MirrorCS");Q39=makeQuery(id+"F17.imprint","IMPRINT",FACE,{"disambiguationData":[TD([[makeQuery(id+"F17.imprint","IMPRINT",EDGE,{"derivedFrom":subQ5}),-1.0]])]});}
            var Q40;
            {var subQ0=sQuery(id+"F17.wireOp",EDGE,"E48");var subQ1=sQuery(id+"F17.wireOp",EDGE,"E39.2");var subQ2=makeQuery(id+"F17.imprint","INTERSECT",VERTEX,{"derivedFrom":[subQ1,subQ0]});Q40=makeQuery(id+"F17.imprint","IMPRINT",FACE,{"disambiguationData":[TD([[makeQuery(id+"F17.imprint","IMPRINT",EDGE,{"disambiguationData":[TD([[subQ2,1.0]])],"derivedFrom":subQ1}),-1.0]])]});}
            var Q41;
            {var subQ0=sQuery(id+"F17.wireOp",EDGE,"E120.MirrorCS");var subQ1=sQuery(id+"F17.wireOp",EDGE,"E98.MirrorCS");var subQ2=makeQuery(id+"F17.imprint","INTERSECT",VERTEX,{"derivedFrom":[subQ1,subQ0]});Q41=makeQuery(id+"F17.imprint","IMPRINT",FACE,{"disambiguationData":[TD([[makeQuery(id+"F17.imprint","IMPRINT",EDGE,{"disambiguationData":[TD([[subQ2,-1.0]])],"derivedFrom":subQ1}),1.0]])]});}
            var Q42;
            {var subQ0=sQuery(id+"F17.wireOp",EDGE,"E120.MirrorCS");var subQ1=sQuery(id+"F17.wireOp",EDGE,"E100.MirrorCS");var subQ2=makeQuery(id+"F17.imprint","INTERSECT",VERTEX,{"derivedFrom":[subQ1,subQ0]});Q42=makeQuery(id+"F17.imprint","IMPRINT",FACE,{"disambiguationData":[TD([[makeQuery(id+"F17.imprint","IMPRINT",EDGE,{"disambiguationData":[TD([[subQ2,-1.0]])],"derivedFrom":subQ1}),1.0]])]});}
            var Q43;
            Q43=makeQuery(id+"F17.imprint","IMPRINT",FACE,{"disambiguationData":[TD([[makeQuery(id+"F17.imprint","IMPRINT",EDGE,{"derivedFrom":sQuery(id+"F17.wireOp",EDGE,"E121.MirrorCS")}),1.0]])]});
            var Q44;
            {var subQ0=sQuery(id+"F17.wireOp",EDGE,"E120.MirrorCS");var subQ1=sQuery(id+"F17.wireOp",EDGE,"E98.MirrorCS");var subQ2=makeQuery(id+"F17.imprint","INTERSECT",VERTEX,{"derivedFrom":[subQ1,subQ0]});Q44=makeQuery(id+"F17.imprint","IMPRINT",FACE,{"disambiguationData":[TD([[makeQuery(id+"F17.imprint","IMPRINT",EDGE,{"disambiguationData":[TD([[subQ2,-1.0]])],"derivedFrom":subQ1}),-1.0]])]});}
            var Q45;
            {var subQ0=sQuery(id+"F17.wireOp",EDGE,"E120.MirrorCS");var subQ1=sQuery(id+"F17.wireOp",EDGE,"E99.MirrorCS");var subQ2=makeQuery(id+"F17.imprint","INTERSECT",VERTEX,{"derivedFrom":[subQ1,subQ0]});Q45=makeQuery(id+"F17.imprint","IMPRINT",FACE,{"disambiguationData":[TD([[makeQuery(id+"F17.imprint","IMPRINT",EDGE,{"disambiguationData":[TD([[subQ2,-1.0]])],"derivedFrom":subQ1}),-1.0]])]});}
            var Q46;
            {var subQ0=sQuery(id+"F17.wireOp",EDGE,"E120.MirrorCS");var subQ1=sQuery(id+"F17.wireOp",EDGE,"E101.MirrorCS");var subQ2=makeQuery(id+"F17.imprint","INTERSECT",VERTEX,{"derivedFrom":[subQ1,subQ0]});Q46=makeQuery(id+"F17.imprint","IMPRINT",FACE,{"disambiguationData":[TD([[makeQuery(id+"F17.imprint","IMPRINT",EDGE,{"disambiguationData":[TD([[subQ2,-1.0]])],"derivedFrom":subQ1}),1.0]])]});}
            var Q47;
            {var subQ6=sQuery(id+"F17.wireOp",EDGE,"E127.MirrorCS");Q47=makeQuery(id+"F17.imprint","IMPRINT",FACE,{"disambiguationData":[TD([[makeQuery(id+"F17.imprint","IMPRINT",EDGE,{"derivedFrom":subQ6}),-1.0]])]});}
            var Q48;
            {var subQ8=sQuery(id+"F17.wireOp",EDGE,"E122.MirrorCS");var subQ10=sQuery(id+"F17.wireOp",EDGE,"E160.MirrorCS");var subQ21=makeQuery(id+"F17.imprint","INTERSECT",VERTEX,{"derivedFrom":[subQ8,subQ10]});Q48=makeQuery(id+"F17.imprint","IMPRINT",FACE,{"disambiguationData":[TD([[makeQuery(id+"F17.imprint","IMPRINT",EDGE,{"disambiguationData":[TD([[subQ21,-1.0]])],"derivedFrom":subQ8}),-1.0]])]});}
            var Q49;
            {var subQ0=sQuery(id+"F17.wireOp",EDGE,"E142.MirrorCS");Q49=makeQuery(id+"F17.imprint","IMPRINT",FACE,{"disambiguationData":[TD([[makeQuery(id+"F17.imprint","IMPRINT",EDGE,{"derivedFrom":subQ0}),-1.0]])]});}
            var Q50;
            {var subQ0=sQuery(id+"F17.wireOp",EDGE,"E141.MirrorCS");Q50=makeQuery(id+"F17.imprint","IMPRINT",FACE,{"disambiguationData":[TD([[makeQuery(id+"F17.imprint","IMPRINT",EDGE,{"derivedFrom":subQ0}),-1.0]])]});}
            var Q51;
            {var subQ0=sQuery(id+"F17.wireOp",EDGE,"E140.MirrorCS");Q51=makeQuery(id+"F17.imprint","IMPRINT",FACE,{"disambiguationData":[TD([[makeQuery(id+"F17.imprint","IMPRINT",EDGE,{"derivedFrom":subQ0}),1.0]])]});}
            var Q52;
            {var subQ0=sQuery(id+"F17.wireOp",EDGE,"E137.MirrorCS");Q52=makeQuery(id+"F17.imprint","IMPRINT",FACE,{"disambiguationData":[TD([[makeQuery(id+"F17.imprint","IMPRINT",EDGE,{"derivedFrom":subQ0}),-1.0]])]});}
            var Q53;
            {var subQ0=sQuery(id+"F17.wireOp",EDGE,"E128.MirrorCS");Q53=makeQuery(id+"F17.imprint","IMPRINT",FACE,{"disambiguationData":[TD([[makeQuery(id+"F17.imprint","IMPRINT",EDGE,{"derivedFrom":subQ0}),-1.0]])]});}
            var Q54;
            {var subQ3=sQuery(id+"F17.wireOp",EDGE,"E131.MirrorCS");Q54=makeQuery(id+"F17.imprint","IMPRINT",FACE,{"disambiguationData":[TD([[makeQuery(id+"F17.imprint","IMPRINT",EDGE,{"derivedFrom":subQ3}),1.0]])]});}
            var Q55;
            {var subQ0=sQuery(id+"F17.wireOp",EDGE,"E133.MirrorCS");Q55=makeQuery(id+"F17.imprint","IMPRINT",FACE,{"disambiguationData":[TD([[makeQuery(id+"F17.imprint","IMPRINT",EDGE,{"derivedFrom":subQ0}),-1.0]])]});}
            var Q56;
            {var subQ0=sQuery(id+"F17.wireOp",EDGE,"E145.MirrorCS");Q56=makeQuery(id+"F17.imprint","IMPRINT",FACE,{"disambiguationData":[TD([[makeQuery(id+"F17.imprint","IMPRINT",EDGE,{"derivedFrom":subQ0}),-1.0]])]});}
            var Q57;
            {var subQ0=sQuery(id+"F17.wireOp",EDGE,"E134.MirrorCS");var subQ1=sQuery(id+"F17.wireOp",EDGE,"E39.2");var subQ2=makeQuery(id+"F17.imprint","INTERSECT",VERTEX,{"derivedFrom":[subQ1,subQ0]});Q57=makeQuery(id+"F17.imprint","IMPRINT",FACE,{"disambiguationData":[TD([[makeQuery(id+"F17.imprint","IMPRINT",EDGE,{"disambiguationData":[TD([[subQ2,-1.0]])],"derivedFrom":subQ1}),-1.0]])]});}
            var Q58;
            {var subQ3=sQuery(id+"F17.wireOp",EDGE,"E123.MirrorCS");var subQ5=sQuery(id+"F17.wireOp",EDGE,"E39.2");var subQ6=makeQuery(id+"F17.imprint","INTERSECT",VERTEX,{"derivedFrom":[subQ5,subQ3]});Q58=makeQuery(id+"F17.imprint","IMPRINT",FACE,{"disambiguationData":[TD([[makeQuery(id+"F17.imprint","IMPRINT",EDGE,{"disambiguationData":[TD([[subQ6,-1.0]])],"derivedFrom":subQ5}),-1.0]])]});}
            extrude(context, id + "F19", {"entities" : qUnion([Q0, Q1, Q2, Q3, Q4, Q5, Q6, Q7, Q8, Q9, Q10, Q11, Q12, Q13, Q14, Q15, Q16, Q17, Q18, Q19, Q20, Q21, Q22, Q23, Q24, Q25, Q26, Q27, Q28, Q29, Q30, Q31, Q32, Q33, Q34, Q35, Q36, Q37, Q38, Q39, Q40, Q41, Q42, Q43, Q44, Q45, Q46, Q47, Q48, Q49, Q50, Q51, Q52, Q53, Q54, Q55, Q56, Q57, Q58]), "operationType" : NewBodyOperationType.ADD, "oppositeDirection" : true, "depth" : 2 * mm, "offsetDistance" : 25 * mm});
        }
        {
            var Q0;
            Q0=makeQuery(id+"F8.boolean.opBoolean","COPY",FACE,{"derivedFrom":makeQuery(id+"F8.opExtrude","SWEPT_FACE",FACE,{"disambiguationData":[OSD([sQuery(id+"F7.wireOp",EDGE,"E14")])]})});
            var sketch = newSketch(context, id + "F20", { "sketchPlane" : qUnion([Q0])});
            skArc(sketch, "E163.0", {"start": v(-135, -157.5) * mm, "mid": v(0, -180.97) * mm, "end": v(135, -157.5) * mm});
            skLineSegment(sketch, "E164", {"start": v(-135, -157.5) * mm, "end": v(-135, -137.5) * mm});
            skLineSegment(sketch, "E165", {"start": v(-135, -137.5) * mm, "end": v(135, -137.5) * mm});
            skLineSegment(sketch, "E166", {"start": v(135, -137.5) * mm, "end": v(135, -157.5) * mm});
            skSolve(sketch);
        }
        {
            var Q0;
            Q0=qSketchRegion(id+"F20",true);
            var Q1;
            Q1=makeQuery(id+"F8.boolean.opBoolean","COPY",FACE,{"derivedFrom":makeQuery(id+"F8.opExtrude","SWEPT_FACE",FACE,{"disambiguationData":[OSD([sQuery(id+"F7.wireOp",EDGE,"E13")])]})});
            extrude(context, id + "F21", {"entities" : qUnion([Q0]), "endBound" : BoundingType.UP_TO_SURFACE, "depth" : 25 * mm, "endBoundEntityFace" : qUnion([Q1]), "offsetDistance" : 25 * mm});
        }
        {
            var Q0;
            Q0=makeQuery(id+"F6.boolean.opBoolean","COPY",FACE,{"derivedFrom":makeQuery(id+"F6.opExtrude","CAP_FACE",FACE,{"disambiguationData":[OSD([sQuery(id+"F5.wireOp",EDGE,"E7.0.2"),sQuery(id+"F5.wireOp",EDGE,"E8"),sQuery(id+"F5.wireOp",EDGE,"E9"),sQuery(id+"F5.wireOp",EDGE,"E10.MirrorCS"),sQuery(id+"F5.wireOp",EDGE,"E11.MirrorCS")])],"isStart":true})});
            cPlane(context, id + "F22", {"entities" : qUnion([Q0]), "cplaneType" : CPlaneType.OFFSET, "offset" : 230 * mm, "width" : 150 * mm, "height" : 150 * mm});
        }
        {
            var Q0;
            Q0=qCreatedBy(id+"F22.planeOp",FACE);
            var sketch = newSketch(context, id + "F23", { "sketchPlane" : qUnion([Q0])});
            skLineSegment(sketch, "E167", {"start": v(0, 33.17) * mm, "end": v(0, -218.1) * mm, "construction": true});
            skLineSegment(sketch, "E168", {"start": v(-50, 0) * mm, "end": v(-50, -209.98) * mm, "construction": true});
            skLineSegment(sketch, "E169.0.0", {"start": v(-90, -129.3) * mm, "end": v(90, -129.3) * mm});
            skLineSegment(sketch, "E169.0.2", {"start": v(90, -129.3) * mm, "end": v(-90, -129.3) * mm});
            skLineSegment(sketch, "E170", {"start": v(-60, -129.3) * mm, "end": v(-56, -163.8) * mm});
            skLineSegment(sketch, "E171", {"start": v(-60.9, -163.8) * mm, "end": v(-38.9, -163.8) * mm});
            skLineSegment(sketch, "E172", {"start": v(-50, -163.8) * mm, "end": v(-50, -129.3) * mm});
            skSolve(sketch);
        }
        {
            var Q0;
            {var subQ0=sQuery(id+"F23.wireOp",EDGE,"E170");Q0=makeQuery(id+"F23.imprint","IMPRINT",FACE,{"disambiguationData":[TD([[makeQuery(id+"F23.imprint","IMPRINT",EDGE,{"derivedFrom":subQ0}),1.0]])]});}
            var Q1;
            Q1=sQuery(id+"F23.wireOp",EDGE,"E172");
            revolve(context, id + "F24", {"surfaceOperationType" : NewSurfaceOperationType.NEW, "entities" : qUnion([Q0]), "axis" : qUnion([Q1]), "revolveType" : RevolveType.FULL});
        }
        {
            var Q0;
            Q0=makeQuery(id+"F24.opRevolve","SWEPT_FACE",FACE,{"disambiguationData":[OSD([sQuery(id+"F23.wireOp",EDGE,"E171")])]});
            var sketch = newSketch(context, id + "F25", { "sketchPlane" : qUnion([Q0])});
            skCircle(sketch, "E173.0", {"center": v(-50, 680) * mm, "radius": 6 * mm, "construction": true});
            skLineSegment(sketch, "E174", {"start": v(-50, 717.97) * mm, "end": v(-50, 638.06) * mm, "construction": true});
            skLineSegment(sketch, "E175.bottom", {"start": v(-60, 695) * mm, "end": v(-40, 695) * mm});
            skLineSegment(sketch, "E175.top", {"start": v(-57, 665) * mm, "end": v(-57, 665) * mm});
            skLineSegment(sketch, "E175.left", {"start": v(-60, 695) * mm, "end": v(-60, 668) * mm});
            skLineSegment(sketch, "E176.top", {"start": v(-54, 655) * mm, "end": v(-46, 655) * mm});
            skLineSegment(sketch, "E176.left", {"start": v(-54, 662) * mm, "end": v(-54, 655) * mm});
            skPoint(sketch, "E177.visualSharp", {"position": v(-60, 665) * mm});
            skArc(sketch, "E177.filletArc", {"start": v(-60, 668) * mm, "mid": v(-59.12, 665.88) * mm, "end": v(-57, 665) * mm});
            skArc(sketch, "E178.filletArc", {"start": v(-54, 662) * mm, "mid": v(-54.88, 664.12) * mm, "end": v(-57, 665) * mm});
            skLineSegment(sketch, "E179", {"start": v(-57, 665) * mm, "end": v(-50, 665) * mm});
            skLineSegment(sketch, "E180", {"start": v(-50, 695) * mm, "end": v(-50, 655) * mm});
            skSolve(sketch);
        }
        {
            var Q0;
            {var subQ1=sQuery(id+"F25.wireOp",EDGE,"E175.left");Q0=makeQuery(id+"F25.imprint","IMPRINT",FACE,{"disambiguationData":[TD([[makeQuery(id+"F25.imprint","IMPRINT",EDGE,{"derivedFrom":subQ1}),1.0]])]});}
            var Q1;
            {var subQ0=sQuery(id+"F25.wireOp",EDGE,"E180");var subQ1=makeQuery(id+"F24.opRevolve","SWEPT_EDGE",EDGE,{"disambiguationData":[OSD([sQuery(id+"F23.wireOp",EDGE,"E170"),sQuery(id+"F23.wireOp",EDGE,"E171")])]});var subQ2=makeQuery(id+"F25.imprint","INTERSECT",VERTEX,{"disambiguationData":[OD(0.0)],"derivedFrom":[subQ1,subQ0]});Q1=makeQuery(id+"F25.imprint","IMPRINT",FACE,{"disambiguationData":[TD([[makeQuery(id+"F25.imprint","IMPRINT",EDGE,{"disambiguationData":[TD([[subQ2,-1.0]])],"derivedFrom":subQ0}),-1.0]])]});}
            var Q2;
            {var subQ1=sQuery(id+"F25.wireOp",EDGE,"E176.left");Q2=makeQuery(id+"F25.imprint","IMPRINT",FACE,{"disambiguationData":[TD([[makeQuery(id+"F25.imprint","IMPRINT",EDGE,{"derivedFrom":subQ1}),1.0]])]});}
            var Q3;
            Q3=sQuery(id+"F25.wireOp",EDGE,"E174");
            revolve(context, id + "F26", {"operationType" : NewBodyOperationType.ADD, "surfaceOperationType" : NewSurfaceOperationType.NEW, "entities" : qUnion([Q0, Q1, Q2]), "axis" : qUnion([Q3]), "revolveType" : RevolveType.FULL});
        }
        {
            var Q0;
            Q0=sQuery(id+"F25.wireOp",VERTEX,"E175.left.start");
            var Q1;
            Q1=sQuery(id+"F25.wireOp",VERTEX,"E177.filletArc.start");
            var Q2;
            Q2=sQuery(id+"F25.wireOp",VERTEX,"E173.0.center");
            cPlane(context, id + "F27", {"entities" : qUnion([Q0, Q1, Q2]), "cplaneType" : CPlaneType.THREE_POINT, "offset" : 25 * mm, "width" : 150 * mm, "height" : 150 * mm});
        }
        {
            var Q0;
            Q0=qCreatedBy(id+"F27.planeOp",FACE);
            var sketch = newSketch(context, id + "F28", { "sketchPlane" : qUnion([Q0])});
            skLineSegment(sketch, "E181.0", {"start": v(40, 695) * mm, "end": v(60, 695) * mm});
            skLineSegment(sketch, "E182", {"start": v(50, 714.18) * mm, "end": v(50, 675.84) * mm, "construction": true});
            skPoint(sketch, "E182.startSnap0", {"position": v(50, 695) * mm});
            skLineSegment(sketch, "E183", {"start": v(48, 695) * mm, "end": v(48, 700) * mm});
            skLineSegment(sketch, "E184", {"start": v(48, 700) * mm, "end": v(42.5, 700) * mm});
            skLineSegment(sketch, "E185", {"start": v(42.5, 700) * mm, "end": v(42.5, 715) * mm});
            skLineSegment(sketch, "E186", {"start": v(42.5, 715) * mm, "end": v(57.5, 715) * mm});
            skLineSegment(sketch, "E187", {"start": v(57.5, 715) * mm, "end": v(57.5, 700) * mm});
            skLineSegment(sketch, "E188", {"start": v(57.5, 700) * mm, "end": v(52, 700) * mm});
            skLineSegment(sketch, "E189", {"start": v(52, 700) * mm, "end": v(52, 695) * mm});
            skLineSegment(sketch, "E190.bottom", {"start": v(44.5, 713) * mm, "end": v(55.5, 713) * mm});
            skLineSegment(sketch, "E190.top", {"start": v(44.5, 702) * mm, "end": v(55.5, 702) * mm});
            skLineSegment(sketch, "E190.left", {"start": v(44.5, 713) * mm, "end": v(44.5, 702) * mm});
            skLineSegment(sketch, "E190.right", {"start": v(55.5, 713) * mm, "end": v(55.5, 702) * mm});
            skSolve(sketch);
        }
        {
            var Q0;
            {var subQ1=sQuery(id+"F28.wireOp",EDGE,"E183");Q0=makeQuery(id+"F28.imprint","IMPRINT",FACE,{"disambiguationData":[TD([[makeQuery(id+"F28.imprint","IMPRINT",EDGE,{"derivedFrom":subQ1}),-1.0]])]});}
            extrude(context, id + "F29", {"entities" : qUnion([Q0]), "operationType" : NewBodyOperationType.ADD, "endBound" : BoundingType.SYMMETRIC, "depth" : 5 * mm, "offsetDistance" : 25 * mm});
        }
        {
            var Q0;
            Q0=makeQuery(id+"F29.opExtrude","SWEPT_EDGE",EDGE,{"disambiguationData":[OSD([sQuery(id+"F28.wireOp",EDGE,"E186"),sQuery(id+"F28.wireOp",EDGE,"E187")])]});
            var Q1;
            Q1=makeQuery(id+"F29.opExtrude","SWEPT_EDGE",EDGE,{"disambiguationData":[OSD([sQuery(id+"F28.wireOp",EDGE,"E187"),sQuery(id+"F28.wireOp",EDGE,"E188")])]});
            var Q2;
            Q2=makeQuery(id+"F29.opExtrude","SWEPT_EDGE",EDGE,{"disambiguationData":[OSD([sQuery(id+"F28.wireOp",EDGE,"E185"),sQuery(id+"F28.wireOp",EDGE,"E186")])]});
            var Q3;
            Q3=makeQuery(id+"F29.opExtrude","SWEPT_EDGE",EDGE,{"disambiguationData":[OSD([sQuery(id+"F28.wireOp",EDGE,"E184"),sQuery(id+"F28.wireOp",EDGE,"E185")])]});
            fillet(context, id + "F30", {"entities" : qUnion([Q0, Q1, Q2, Q3]), "radius" : 3 * mm, "tangentPropagation" : true, "allowEdgeOverflow" : false});
        }
        {
            var Q0;
            Q0=makeQuery(id+"F29.opExtrude","SWEPT_EDGE",EDGE,{"disambiguationData":[OSD([sQuery(id+"F28.wireOp",EDGE,"E190.bottom"),sQuery(id+"F28.wireOp",EDGE,"E190.right")])]});
            var Q1;
            Q1=makeQuery(id+"F29.opExtrude","SWEPT_EDGE",EDGE,{"disambiguationData":[OSD([sQuery(id+"F28.wireOp",EDGE,"E190.bottom"),sQuery(id+"F28.wireOp",EDGE,"E190.left")])]});
            var Q2;
            Q2=makeQuery(id+"F29.opExtrude","SWEPT_EDGE",EDGE,{"disambiguationData":[OSD([sQuery(id+"F28.wireOp",EDGE,"E190.top"),sQuery(id+"F28.wireOp",EDGE,"E190.left")])]});
            var Q3;
            Q3=makeQuery(id+"F29.opExtrude","SWEPT_EDGE",EDGE,{"disambiguationData":[OSD([sQuery(id+"F28.wireOp",EDGE,"E190.top"),sQuery(id+"F28.wireOp",EDGE,"E190.right")])]});
            fillet(context, id + "F31", {"entities" : qUnion([Q0, Q1, Q2, Q3]), "radius" : 1 * mm, "tangentPropagation" : true, "allowEdgeOverflow" : false});
        }
        {
            var Q0;
            Q0=makeQuery(id+"F24.opRevolve","SWEPT_BODY",BODY,{"disambiguationData":[OSD([sQuery(id+"F23.wireOp",EDGE,"E169.0.2"),sQuery(id+"F23.wireOp",EDGE,"E170"),sQuery(id+"F23.wireOp",EDGE,"E171"),sQuery(id+"F23.wireOp",EDGE,"E172")])]});
            var Q1;
            Q1=qCreatedBy(makeId("Right.planeOp"),FACE);
            mirror(context, id + "F32", {"entities" : qUnion([Q0]), "mirrorPlane" : qUnion([Q1])});
        }
        {
            var Q0;
            Q0=qCreatedBy(makeId("Right.planeOp"),FACE);
            cPlane(context, id + "F33", {"entities" : qUnion([Q0]), "cplaneType" : CPlaneType.OFFSET, "offset" : (315 / 2 - 50) * mm, "width" : 150 * mm, "height" : 150 * mm});
        }
        {
            var Q0;
            Q0=qCreatedBy(id+"F33.planeOp",FACE);
            var sketch = newSketch(context, id + "F34", { "sketchPlane" : qUnion([Q0])});
            skLineSegment(sketch, "E191.0", {"start": v(157.5, 955) * mm, "end": v(157.5, 0) * mm});
            skLineSegment(sketch, "E192", {"start": v(157.5, 920) * mm, "end": v(166.5, 920) * mm});
            skLineSegment(sketch, "E193", {"start": v(166.5, 920) * mm, "end": v(157.5, 904.41) * mm});
            skLineSegment(sketch, "E194", {"start": v(157.5, 904.41) * mm, "end": v(157.5, 886.41) * mm});
            skLineSegment(sketch, "E195", {"start": v(157.5, 886.41) * mm, "end": v(149.5, 886.41) * mm});
            skLineSegment(sketch, "E196", {"start": v(149.5, 886.41) * mm, "end": v(149.5, 920) * mm});
            skLineSegment(sketch, "E197", {"start": v(149.5, 920) * mm, "end": v(157.5, 920) * mm});
            skSolve(sketch);
        }
        {
            var Q0;
            {var subQ4=sQuery(id+"F34.wireOp",EDGE,"E192");var subQ6=sQuery(id+"F34.wireOp",EDGE,"E195");Q0=qUnion([makeQuery(id+"F34.imprint","IMPRINT",FACE,{"disambiguationData":[TD([[makeQuery(id+"F34.imprint","IMPRINT",EDGE,{"derivedFrom":subQ6}),-1.0]])]}),makeQuery(id+"F34.imprint","IMPRINT",FACE,{"disambiguationData":[TD([[makeQuery(id+"F34.imprint","IMPRINT",EDGE,{"derivedFrom":subQ4}),-1.0]])]})]);}
            extrude(context, id + "F35", {"entities" : qUnion([Q0]), "operationType" : NewBodyOperationType.REMOVE, "endBound" : BoundingType.SYMMETRIC, "oppositeDirection" : true, "depth" : 10 * mm, "offsetDistance" : 25 * mm});
        }
        {
            var Q0;
            Q0=qCreatedBy(id+"F33.planeOp",FACE);
            cPlane(context, id + "F36", {"entities" : qUnion([Q0]), "cplaneType" : CPlaneType.OFFSET, "offset" : 20 * mm, "oppositeDirection" : true, "width" : 150 * mm, "height" : 150 * mm});
        }
        {
            var Q0;
            Q0=qCreatedBy(id+"F36.planeOp",FACE);
            var sketch = newSketch(context, id + "F37", { "sketchPlane" : qUnion([Q0])});
            skLineSegment(sketch, "E198.0", {"start": v(157.5, 886.41) * mm, "end": v(149.5, 886.41) * mm});
            skLineSegment(sketch, "E198.1", {"start": v(149.5, 886.41) * mm, "end": v(149.5, 920) * mm});
            skLineSegment(sketch, "E198.2", {"start": v(149.5, 920) * mm, "end": v(157.5, 920) * mm});
            skLineSegment(sketch, "E198.3", {"start": v(157.5, 920) * mm, "end": v(166.5, 920) * mm});
            skLineSegment(sketch, "E198.4", {"start": v(166.5, 920) * mm, "end": v(157.5, 904.41) * mm});
            skLineSegment(sketch, "E198.5", {"start": v(157.5, 904.41) * mm, "end": v(157.5, 886.41) * mm});
            skSolve(sketch);
        }
        {
            var Q0;
            Q0=qSketchRegion(id+"F37",true);
            extrude(context, id + "F38", {"entities" : qUnion([Q0]), "operationType" : NewBodyOperationType.REMOVE, "endBound" : BoundingType.SYMMETRIC, "oppositeDirection" : true, "depth" : 10 * mm, "offsetDistance" : 25 * mm});
        }
        {
            var Q0;
            {var subQ4=sQuery(id+"F34.wireOp",EDGE,"E192");var subQ6=sQuery(id+"F34.wireOp",EDGE,"E195");Q0=qUnion([makeQuery(id+"F34.imprint","IMPRINT",FACE,{"disambiguationData":[TD([[makeQuery(id+"F34.imprint","IMPRINT",EDGE,{"derivedFrom":subQ6}),-1.0]])]}),makeQuery(id+"F34.imprint","IMPRINT",FACE,{"disambiguationData":[TD([[makeQuery(id+"F34.imprint","IMPRINT",EDGE,{"derivedFrom":subQ4}),-1.0]])]})]);}
            extrude(context, id + "F39", {"entities" : qUnion([Q0]), "endBound" : BoundingType.SYMMETRIC, "depth" : 10 * mm, "offsetDistance" : 25 * mm});
        }
        {
            var Q0;
            Q0=qSketchRegion(id+"F37",true);
            extrude(context, id + "F40", {"entities" : qUnion([Q0]), "endBound" : BoundingType.SYMMETRIC, "depth" : 10 * mm, "offsetDistance" : 25 * mm});
        }
        {
            var Q0;
            {var subQ0=sQuery(id+"F0.wireOp",EDGE,"E0.left");var subQ1=sQuery(id+"F0.wireOp",EDGE,"E0.bottom");Q0=makeQuery(id+"F13.opFillet","BLEND_VERTEX",VERTEX,{"blendedFrom":[makeQuery(id+"F1.opExtrude","CAP_VERTEX",VERTEX,{"disambiguationData":[OSD([subQ1,subQ0])],"isStart":false}),makeQuery(id+"F1.opExtrude","SWEPT_EDGE",EDGE,{"disambiguationData":[OSD([subQ1,subQ0])]}),makeQuery(id+"F1.opExtrude","CAP_EDGE",EDGE,{"disambiguationData":[OSD([subQ0])],"isStart":false}),makeQuery(id+"F1.opExtrude","SWEPT_FACE",FACE,{"disambiguationData":[OSD([subQ0])]})],"blendedInto":[makeQuery(id+"F1.opExtrude","SWEPT_FACE",FACE,{"disambiguationData":[OSD([subQ0])]})]});}
            var Q1;
            {var subQ0=sQuery(id+"F0.wireOp",EDGE,"E1");var subQ1=sQuery(id+"F0.wireOp",EDGE,"E0.top");var subQ2=sQuery(id+"F0.wireOp",EDGE,"E0.left");var subQ3=makeQuery(id+"F1.opExtrude","SWEPT_FACE",FACE,{"disambiguationData":[OSD([subQ2])]});var subQ4=sQuery(id+"F0.wireOp",EDGE,"E0.bottom");Q1=makeQuery(id+"F13.opFillet","BLEND_VERTEX",VERTEX,{"blendedFrom":[makeQuery(id+"F1.opExtrude","SWEPT_EDGE",EDGE,{"disambiguationData":[OSD([subQ4,subQ2])]}),subQ3,makeQuery(id+"F10.boolean.opBoolean","SPLIT",FACE,{"disambiguationData":[TD([subQ3])],"derivedFrom":makeQuery(id+"F1.opExtrude","CAP_FACE",FACE,{"disambiguationData":[OSD([subQ4,subQ1,subQ2,sQuery(id+"F0.wireOp",EDGE,"E0.right"),subQ0])],"isStart":true})})],"blendedInto":[subQ3,makeQuery(id+"F10.boolean.opBoolean","SPLIT",FACE,{"disambiguationData":[TD([subQ3])],"derivedFrom":makeQuery(id+"F1.opExtrude","CAP_FACE",FACE,{"disambiguationData":[OSD([subQ4,subQ1,subQ2,sQuery(id+"F0.wireOp",EDGE,"E0.right"),subQ0])],"isStart":true})})]});}
            var Q2;
            {var subQ0=sQuery(id+"F0.wireOp",EDGE,"E0.right");var subQ1=sQuery(id+"F0.wireOp",EDGE,"E0.bottom");Q2=makeQuery(id+"F13.opFillet","BLEND_VERTEX",VERTEX,{"blendedFrom":[makeQuery(id+"F1.opExtrude","CAP_VERTEX",VERTEX,{"disambiguationData":[OSD([subQ1,subQ0])],"isStart":false}),makeQuery(id+"F1.opExtrude","SWEPT_EDGE",EDGE,{"disambiguationData":[OSD([subQ1,subQ0])]}),makeQuery(id+"F1.opExtrude","CAP_EDGE",EDGE,{"disambiguationData":[OSD([subQ0])],"isStart":false}),makeQuery(id+"F1.opExtrude","SWEPT_FACE",FACE,{"disambiguationData":[OSD([subQ0])]})],"blendedInto":[makeQuery(id+"F1.opExtrude","SWEPT_FACE",FACE,{"disambiguationData":[OSD([subQ0])]})]});}
            cPlane(context, id + "F41", {"entities" : qUnion([Q0, Q1, Q2]), "cplaneType" : CPlaneType.THREE_POINT, "offset" : 25 * mm, "width" : 150 * mm, "height" : 150 * mm});
        }
        {
            var Q0;
            Q0=qCreatedBy(id+"F41.planeOp",FACE);
            var sketch = newSketch(context, id + "F42", { "sketchPlane" : qUnion([Q0])});
            skLineSegment(sketch, "E199.bottom", {"start": v(-125, 945) * mm, "end": v(125, 945) * mm});
            skLineSegment(sketch, "E199.top", {"start": v(-125, 855) * mm, "end": v(125, 855) * mm});
            skLineSegment(sketch, "E199.left", {"start": v(-125, 945) * mm, "end": v(-125, 855) * mm});
            skLineSegment(sketch, "E199.right", {"start": v(125, 945) * mm, "end": v(125, 855) * mm});
            skSolve(sketch);
        }
        {
            var Q0;
            Q0=qSketchRegion(id+"F42",true);
            extrude(context, id + "F43", {"entities" : qUnion([Q0]), "operationType" : NewBodyOperationType.REMOVE, "endBound" : BoundingType.THROUGH_ALL, "depth" : 25 * mm, "offsetDistance" : 25 * mm});
        }
        {
            var Q0;
            Q0=makeQuery(id+"F43.boolean.opBoolean","COPY",FACE,{"derivedFrom":makeQuery(id+"F43.opExtrude","CAP_FACE",FACE,{"disambiguationData":[OSD([sQuery(id+"F42.wireOp",EDGE,"E199.bottom"),sQuery(id+"F42.wireOp",EDGE,"E199.top"),sQuery(id+"F42.wireOp",EDGE,"E199.left"),sQuery(id+"F42.wireOp",EDGE,"E199.right")])],"isStart":true})});
            var sketch = newSketch(context, id + "F44", { "sketchPlane" : qUnion([Q0])});
            skLineSegment(sketch, "E200.bottom", {"start": v(-125, 945) * mm, "end": v(125, 945) * mm});
            skLineSegment(sketch, "E200.top", {"start": v(-125, 855) * mm, "end": v(125, 855) * mm});
            skLineSegment(sketch, "E200.left", {"start": v(-125, 945) * mm, "end": v(-125, 855) * mm});
            skLineSegment(sketch, "E200.right", {"start": v(125, 945) * mm, "end": v(125, 855) * mm});
            skLineSegment(sketch, "E201.bottom", {"start": v(75, 930) * mm, "end": v(85, 930) * mm});
            skLineSegment(sketch, "E201.top", {"start": v(75, 925) * mm, "end": v(85, 925) * mm});
            skLineSegment(sketch, "E201.left", {"start": v(75, 930) * mm, "end": v(75, 925) * mm});
            skLineSegment(sketch, "E201.right", {"start": v(85, 930) * mm, "end": v(85, 925) * mm});
            skLineSegment(sketch, "E202.bottom", {"start": v(75, 920) * mm, "end": v(85, 920) * mm});
            skLineSegment(sketch, "E202.top", {"start": v(75, 915) * mm, "end": v(85, 915) * mm});
            skLineSegment(sketch, "E202.left", {"start": v(75, 920) * mm, "end": v(75, 915) * mm});
            skLineSegment(sketch, "E202.right", {"start": v(85, 920) * mm, "end": v(85, 915) * mm});
            skSolve(sketch);
        }
        {
            var Q0;
            Q0=makeQuery(id+"F44.imprint","IMPRINT",FACE,{"disambiguationData":[TD([[makeQuery(id+"F44.imprint","IMPRINT",EDGE,{"derivedFrom":sQuery(id+"F44.wireOp",EDGE,"E200.bottom")}),-1.0]])]});
            var Q1;
            Q1=makeQuery(id+"F44.imprint","IMPRINT",FACE,{"disambiguationData":[TD([[makeQuery(id+"F44.imprint","IMPRINT",EDGE,{"derivedFrom":sQuery(id+"F44.wireOp",EDGE,"6fba481b-f54a-40dc-850f-529da61e2d5d.sketch_text.stroke-14")}),1.0]])]});
            var Q2;
            Q2=makeQuery(id+"F44.imprint","IMPRINT",FACE,{"disambiguationData":[TD([[makeQuery(id+"F44.imprint","IMPRINT",EDGE,{"derivedFrom":sQuery(id+"F44.wireOp",EDGE,"6fba481b-f54a-40dc-850f-529da61e2d5d.sketch_text.stroke-50")}),1.0]])]});
            var Q3;
            Q3=makeQuery(id+"F44.imprint","IMPRINT",FACE,{"disambiguationData":[TD([[makeQuery(id+"F44.imprint","IMPRINT",EDGE,{"derivedFrom":sQuery(id+"F44.wireOp",EDGE,"0e071c30-8112-48db-a0b7-94a150164aee.sketch_text.stroke-20")}),1.0]])]});
            var Q4;
            Q4=makeQuery(id+"F44.imprint","IMPRINT",FACE,{"disambiguationData":[TD([[makeQuery(id+"F44.imprint","IMPRINT",EDGE,{"derivedFrom":sQuery(id+"F44.wireOp",EDGE,"e2d7af9a-f6d1-4b82-89d6-a8a0b8d7c55a.sketch_text.stroke-23")}),1.0]])]});
            var Q5;
            Q5=makeQuery(id+"F44.imprint","IMPRINT",FACE,{"disambiguationData":[TD([[makeQuery(id+"F44.imprint","IMPRINT",EDGE,{"derivedFrom":sQuery(id+"F44.wireOp",EDGE,"e2d7af9a-f6d1-4b82-89d6-a8a0b8d7c55a.sketch_text.stroke-44")}),1.0]])]});
            var Q6;
            {var subQ0=sQuery(id+"F0.wireOp",EDGE,"E0.right");var subQ1=sQuery(id+"F0.wireOp",EDGE,"E0.bottom");var subQ2=sQuery(id+"F0.wireOp",EDGE,"E1");var subQ4=sQuery(id+"F0.wireOp",EDGE,"E0.left");Q6=makeQuery(id+"F6.boolean.opBoolean","SPLIT",FACE,{"disambiguationData":[TD([makeQuery(id+"F1.opExtrude","CAP_FACE",FACE,{"disambiguationData":[OSD([subQ1,sQuery(id+"F0.wireOp",EDGE,"E0.top"),subQ4,subQ0,subQ2])],"isStart":false})])],"derivedFrom":makeQuery(id+"F1.opExtrude","SWEPT_FACE",FACE,{"disambiguationData":[OSD([subQ2])]})});}
            extrude(context, id + "F45", {"entities" : qUnion([Q0, Q1, Q2, Q3, Q4, Q5]), "operationType" : NewBodyOperationType.ADD, "endBound" : BoundingType.UP_TO_SURFACE, "depth" : 25 * mm, "endBoundEntityFace" : qUnion([Q6]), "offsetDistance" : 25 * mm});
        }
        {
            var Q0;
            Q0=makeQuery(id+"F44.imprint","IMPRINT",FACE,{"disambiguationData":[TD([[makeQuery(id+"F44.imprint","IMPRINT",EDGE,{"derivedFrom":sQuery(id+"F44.wireOp",EDGE,"E201.bottom")}),-1.0]])]});
            var Q1;
            {var subQ0=sQuery(id+"F0.wireOp",EDGE,"E0.right");var subQ1=sQuery(id+"F0.wireOp",EDGE,"E0.bottom");var subQ2=sQuery(id+"F0.wireOp",EDGE,"E1");var subQ4=sQuery(id+"F0.wireOp",EDGE,"E0.left");Q1=makeQuery(id+"F45.boolean.opBoolean","MERGE",FACE,{"derivedFrom":[makeQuery(id+"F6.boolean.opBoolean","SPLIT",FACE,{"disambiguationData":[TD([makeQuery(id+"F1.opExtrude","CAP_FACE",FACE,{"disambiguationData":[OSD([subQ1,sQuery(id+"F0.wireOp",EDGE,"E0.top"),subQ4,subQ0,subQ2])],"isStart":false})])],"derivedFrom":makeQuery(id+"F1.opExtrude","SWEPT_FACE",FACE,{"disambiguationData":[OSD([subQ2])]})}),makeQuery(id+"F45.opExtrude","CAP_FACE",FACE,{"disambiguationData":[OSD([sQuery(id+"F44.wireOp",EDGE,"E200.bottom"),sQuery(id+"F44.wireOp",EDGE,"E200.top"),sQuery(id+"F44.wireOp",EDGE,"E200.left"),sQuery(id+"F44.wireOp",EDGE,"E200.right"),sQuery(id+"F44.wireOp",EDGE,"E201.bottom"),sQuery(id+"F44.wireOp",EDGE,"E201.top"),sQuery(id+"F44.wireOp",EDGE,"E201.left"),sQuery(id+"F44.wireOp",EDGE,"E201.right"),sQuery(id+"F44.wireOp",EDGE,"E202.bottom"),sQuery(id+"F44.wireOp",EDGE,"E202.top"),sQuery(id+"F44.wireOp",EDGE,"E202.left"),sQuery(id+"F44.wireOp",EDGE,"E202.right"),sQuery(id+"F44.wireOp",EDGE,"0e071c30-8112-48db-a0b7-94a150164aee.sketch_text.stroke-0"),sQuery(id+"F44.wireOp",EDGE,"0e071c30-8112-48db-a0b7-94a150164aee.sketch_text.stroke-1"),sQuery(id+"F44.wireOp",EDGE,"0e071c30-8112-48db-a0b7-94a150164aee.sketch_text.stroke-2"),sQuery(id+"F44.wireOp",EDGE,"0e071c30-8112-48db-a0b7-94a150164aee.sketch_text.stroke-3"),sQuery(id+"F44.wireOp",EDGE,"0e071c30-8112-48db-a0b7-94a150164aee.sketch_text.stroke-4"),sQuery(id+"F44.wireOp",EDGE,"0e071c30-8112-48db-a0b7-94a150164aee.sketch_text.stroke-5"),sQuery(id+"F44.wireOp",EDGE,"0e071c30-8112-48db-a0b7-94a150164aee.sketch_text.stroke-6"),sQuery(id+"F44.wireOp",EDGE,"0e071c30-8112-48db-a0b7-94a150164aee.sketch_text.stroke-7"),sQuery(id+"F44.wireOp",EDGE,"0e071c30-8112-48db-a0b7-94a150164aee.sketch_text.stroke-8"),sQuery(id+"F44.wireOp",EDGE,"0e071c30-8112-48db-a0b7-94a150164aee.sketch_text.stroke-9"),sQuery(id+"F44.wireOp",EDGE,"0e071c30-8112-48db-a0b7-94a150164aee.sketch_text.stroke-10"),sQuery(id+"F44.wireOp",EDGE,"0e071c30-8112-48db-a0b7-94a150164aee.sketch_text.stroke-11"),sQuery(id+"F44.wireOp",EDGE,"0e071c30-8112-48db-a0b7-94a150164aee.sketch_text.stroke-12"),sQuery(id+"F44.wireOp",EDGE,"0e071c30-8112-48db-a0b7-94a150164aee.sketch_text.stroke-13"),sQuery(id+"F44.wireOp",EDGE,"0e071c30-8112-48db-a0b7-94a150164aee.sketch_text.stroke-14"),sQuery(id+"F44.wireOp",EDGE,"0e071c30-8112-48db-a0b7-94a150164aee.sketch_text.stroke-15"),sQuery(id+"F44.wireOp",EDGE,"0e071c30-8112-48db-a0b7-94a150164aee.sketch_text.stroke-16"),sQuery(id+"F44.wireOp",EDGE,"0e071c30-8112-48db-a0b7-94a150164aee.sketch_text.stroke-17"),sQuery(id+"F44.wireOp",EDGE,"0e071c30-8112-48db-a0b7-94a150164aee.sketch_text.stroke-18"),sQuery(id+"F44.wireOp",EDGE,"0e071c30-8112-48db-a0b7-94a150164aee.sketch_text.stroke-19"),sQuery(id+"F44.wireOp",EDGE,"0e071c30-8112-48db-a0b7-94a150164aee.sketch_text.stroke-28"),sQuery(id+"F44.wireOp",EDGE,"0e071c30-8112-48db-a0b7-94a150164aee.sketch_text.stroke-29"),sQuery(id+"F44.wireOp",EDGE,"0e071c30-8112-48db-a0b7-94a150164aee.sketch_text.stroke-30"),sQuery(id+"F44.wireOp",EDGE,"0e071c30-8112-48db-a0b7-94a150164aee.sketch_text.stroke-31"),sQuery(id+"F44.wireOp",EDGE,"0e071c30-8112-48db-a0b7-94a150164aee.sketch_text.stroke-32"),sQuery(id+"F44.wireOp",EDGE,"0e071c30-8112-48db-a0b7-94a150164aee.sketch_text.stroke-33"),sQuery(id+"F44.wireOp",EDGE,"0e071c30-8112-48db-a0b7-94a150164aee.sketch_text.stroke-34"),sQuery(id+"F44.wireOp",EDGE,"0e071c30-8112-48db-a0b7-94a150164aee.sketch_text.stroke-35"),sQuery(id+"F44.wireOp",EDGE,"e2d7af9a-f6d1-4b82-89d6-a8a0b8d7c55a.sketch_text.stroke-0"),sQuery(id+"F44.wireOp",EDGE,"e2d7af9a-f6d1-4b82-89d6-a8a0b8d7c55a.sketch_text.stroke-1"),sQuery(id+"F44.wireOp",EDGE,"e2d7af9a-f6d1-4b82-89d6-a8a0b8d7c55a.sketch_text.stroke-2"),sQuery(id+"F44.wireOp",EDGE,"e2d7af9a-f6d1-4b82-89d6-a8a0b8d7c55a.sketch_text.stroke-3"),sQuery(id+"F44.wireOp",EDGE,"e2d7af9a-f6d1-4b82-89d6-a8a0b8d7c55a.sketch_text.stroke-4"),sQuery(id+"F44.wireOp",EDGE,"e2d7af9a-f6d1-4b82-89d6-a8a0b8d7c55a.sketch_text.stroke-5"),sQuery(id+"F44.wireOp",EDGE,"e2d7af9a-f6d1-4b82-89d6-a8a0b8d7c55a.sketch_text.stroke-6"),sQuery(id+"F44.wireOp",EDGE,"e2d7af9a-f6d1-4b82-89d6-a8a0b8d7c55a.sketch_text.stroke-7"),sQuery(id+"F44.wireOp",EDGE,"e2d7af9a-f6d1-4b82-89d6-a8a0b8d7c55a.sketch_text.stroke-8"),sQuery(id+"F44.wireOp",EDGE,"e2d7af9a-f6d1-4b82-89d6-a8a0b8d7c55a.sketch_text.stroke-9"),sQuery(id+"F44.wireOp",EDGE,"e2d7af9a-f6d1-4b82-89d6-a8a0b8d7c55a.sketch_text.stroke-10"),sQuery(id+"F44.wireOp",EDGE,"e2d7af9a-f6d1-4b82-89d6-a8a0b8d7c55a.sketch_text.stroke-11"),sQuery(id+"F44.wireOp",EDGE,"e2d7af9a-f6d1-4b82-89d6-a8a0b8d7c55a.sketch_text.stroke-12"),sQuery(id+"F44.wireOp",EDGE,"e2d7af9a-f6d1-4b82-89d6-a8a0b8d7c55a.sketch_text.stroke-13"),sQuery(id+"F44.wireOp",EDGE,"e2d7af9a-f6d1-4b82-89d6-a8a0b8d7c55a.sketch_text.stroke-14"),sQuery(id+"F44.wireOp",EDGE,"e2d7af9a-f6d1-4b82-89d6-a8a0b8d7c55a.sketch_text.stroke-15"),sQuery(id+"F44.wireOp",EDGE,"e2d7af9a-f6d1-4b82-89d6-a8a0b8d7c55a.sketch_text.stroke-16"),sQuery(id+"F44.wireOp",EDGE,"e2d7af9a-f6d1-4b82-89d6-a8a0b8d7c55a.sketch_text.stroke-17"),sQuery(id+"F44.wireOp",EDGE,"e2d7af9a-f6d1-4b82-89d6-a8a0b8d7c55a.sketch_text.stroke-18"),sQuery(id+"F44.wireOp",EDGE,"e2d7af9a-f6d1-4b82-89d6-a8a0b8d7c55a.sketch_text.stroke-19"),sQuery(id+"F44.wireOp",EDGE,"e2d7af9a-f6d1-4b82-89d6-a8a0b8d7c55a.sketch_text.stroke-20"),sQuery(id+"F44.wireOp",EDGE,"e2d7af9a-f6d1-4b82-89d6-a8a0b8d7c55a.sketch_text.stroke-21"),sQuery(id+"F44.wireOp",EDGE,"e2d7af9a-f6d1-4b82-89d6-a8a0b8d7c55a.sketch_text.stroke-22"),sQuery(id+"F44.wireOp",EDGE,"e2d7af9a-f6d1-4b82-89d6-a8a0b8d7c55a.sketch_text.stroke-31"),sQuery(id+"F44.wireOp",EDGE,"e2d7af9a-f6d1-4b82-89d6-a8a0b8d7c55a.sketch_text.stroke-32"),sQuery(id+"F44.wireOp",EDGE,"e2d7af9a-f6d1-4b82-89d6-a8a0b8d7c55a.sketch_text.stroke-33"),sQuery(id+"F44.wireOp",EDGE,"e2d7af9a-f6d1-4b82-89d6-a8a0b8d7c55a.sketch_text.stroke-34"),sQuery(id+"F44.wireOp",EDGE,"e2d7af9a-f6d1-4b82-89d6-a8a0b8d7c55a.sketch_text.stroke-35"),sQuery(id+"F44.wireOp",EDGE,"e2d7af9a-f6d1-4b82-89d6-a8a0b8d7c55a.sketch_text.stroke-36"),sQuery(id+"F44.wireOp",EDGE,"e2d7af9a-f6d1-4b82-89d6-a8a0b8d7c55a.sketch_text.stroke-37"),sQuery(id+"F44.wireOp",EDGE,"e2d7af9a-f6d1-4b82-89d6-a8a0b8d7c55a.sketch_text.stroke-38"),sQuery(id+"F44.wireOp",EDGE,"e2d7af9a-f6d1-4b82-89d6-a8a0b8d7c55a.sketch_text.stroke-39"),sQuery(id+"F44.wireOp",EDGE,"e2d7af9a-f6d1-4b82-89d6-a8a0b8d7c55a.sketch_text.stroke-40"),sQuery(id+"F44.wireOp",EDGE,"e2d7af9a-f6d1-4b82-89d6-a8a0b8d7c55a.sketch_text.stroke-41"),sQuery(id+"F44.wireOp",EDGE,"e2d7af9a-f6d1-4b82-89d6-a8a0b8d7c55a.sketch_text.stroke-42"),sQuery(id+"F44.wireOp",EDGE,"e2d7af9a-f6d1-4b82-89d6-a8a0b8d7c55a.sketch_text.stroke-43"),sQuery(id+"F44.wireOp",EDGE,"6fba481b-f54a-40dc-850f-529da61e2d5d.sketch_text.stroke-0"),sQuery(id+"F44.wireOp",EDGE,"6fba481b-f54a-40dc-850f-529da61e2d5d.sketch_text.stroke-1"),sQuery(id+"F44.wireOp",EDGE,"6fba481b-f54a-40dc-850f-529da61e2d5d.sketch_text.stroke-2"),sQuery(id+"F44.wireOp",EDGE,"6fba481b-f54a-40dc-850f-529da61e2d5d.sketch_text.stroke-3"),sQuery(id+"F44.wireOp",EDGE,"6fba481b-f54a-40dc-850f-529da61e2d5d.sketch_text.stroke-4"),sQuery(id+"F44.wireOp",EDGE,"6fba481b-f54a-40dc-850f-529da61e2d5d.sketch_text.stroke-5"),sQuery(id+"F44.wireOp",EDGE,"6fba481b-f54a-40dc-850f-529da61e2d5d.sketch_text.stroke-6"),sQuery(id+"F44.wireOp",EDGE,"6fba481b-f54a-40dc-850f-529da61e2d5d.sketch_text.stroke-7"),sQuery(id+"F44.wireOp",EDGE,"6fba481b-f54a-40dc-850f-529da61e2d5d.sketch_text.stroke-8"),sQuery(id+"F44.wireOp",EDGE,"6fba481b-f54a-40dc-850f-529da61e2d5d.sketch_text.stroke-9"),sQuery(id+"F44.wireOp",EDGE,"6fba481b-f54a-40dc-850f-529da61e2d5d.sketch_text.stroke-10"),sQuery(id+"F44.wireOp",EDGE,"6fba481b-f54a-40dc-850f-529da61e2d5d.sketch_text.stroke-11"),sQuery(id+"F44.wireOp",EDGE,"6fba481b-f54a-40dc-850f-529da61e2d5d.sketch_text.stroke-12"),sQuery(id+"F44.wireOp",EDGE,"6fba481b-f54a-40dc-850f-529da61e2d5d.sketch_text.stroke-13"),sQuery(id+"F44.wireOp",EDGE,"6fba481b-f54a-40dc-850f-529da61e2d5d.sketch_text.stroke-22"),sQuery(id+"F44.wireOp",EDGE,"6fba481b-f54a-40dc-850f-529da61e2d5d.sketch_text.stroke-23"),sQuery(id+"F44.wireOp",EDGE,"6fba481b-f54a-40dc-850f-529da61e2d5d.sketch_text.stroke-24"),sQuery(id+"F44.wireOp",EDGE,"6fba481b-f54a-40dc-850f-529da61e2d5d.sketch_text.stroke-25"),sQuery(id+"F44.wireOp",EDGE,"6fba481b-f54a-40dc-850f-529da61e2d5d.sketch_text.stroke-26"),sQuery(id+"F44.wireOp",EDGE,"6fba481b-f54a-40dc-850f-529da61e2d5d.sketch_text.stroke-27"),sQuery(id+"F44.wireOp",EDGE,"6fba481b-f54a-40dc-850f-529da61e2d5d.sketch_text.stroke-28"),sQuery(id+"F44.wireOp",EDGE,"6fba481b-f54a-40dc-850f-529da61e2d5d.sketch_text.stroke-29"),sQuery(id+"F44.wireOp",EDGE,"6fba481b-f54a-40dc-850f-529da61e2d5d.sketch_text.stroke-30"),sQuery(id+"F44.wireOp",EDGE,"6fba481b-f54a-40dc-850f-529da61e2d5d.sketch_text.stroke-31"),sQuery(id+"F44.wireOp",EDGE,"6fba481b-f54a-40dc-850f-529da61e2d5d.sketch_text.stroke-32"),sQuery(id+"F44.wireOp",EDGE,"6fba481b-f54a-40dc-850f-529da61e2d5d.sketch_text.stroke-33"),sQuery(id+"F44.wireOp",EDGE,"6fba481b-f54a-40dc-850f-529da61e2d5d.sketch_text.stroke-34"),sQuery(id+"F44.wireOp",EDGE,"6fba481b-f54a-40dc-850f-529da61e2d5d.sketch_text.stroke-35"),sQuery(id+"F44.wireOp",EDGE,"6fba481b-f54a-40dc-850f-529da61e2d5d.sketch_text.stroke-36"),sQuery(id+"F44.wireOp",EDGE,"6fba481b-f54a-40dc-850f-529da61e2d5d.sketch_text.stroke-37"),sQuery(id+"F44.wireOp",EDGE,"6fba481b-f54a-40dc-850f-529da61e2d5d.sketch_text.stroke-38"),sQuery(id+"F44.wireOp",EDGE,"6fba481b-f54a-40dc-850f-529da61e2d5d.sketch_text.stroke-39"),sQuery(id+"F44.wireOp",EDGE,"6fba481b-f54a-40dc-850f-529da61e2d5d.sketch_text.stroke-40"),sQuery(id+"F44.wireOp",EDGE,"6fba481b-f54a-40dc-850f-529da61e2d5d.sketch_text.stroke-41"),sQuery(id+"F44.wireOp",EDGE,"6fba481b-f54a-40dc-850f-529da61e2d5d.sketch_text.stroke-42"),sQuery(id+"F44.wireOp",EDGE,"6fba481b-f54a-40dc-850f-529da61e2d5d.sketch_text.stroke-43"),sQuery(id+"F44.wireOp",EDGE,"6fba481b-f54a-40dc-850f-529da61e2d5d.sketch_text.stroke-44"),sQuery(id+"F44.wireOp",EDGE,"6fba481b-f54a-40dc-850f-529da61e2d5d.sketch_text.stroke-45"),sQuery(id+"F44.wireOp",EDGE,"6fba481b-f54a-40dc-850f-529da61e2d5d.sketch_text.stroke-46"),sQuery(id+"F44.wireOp",EDGE,"6fba481b-f54a-40dc-850f-529da61e2d5d.sketch_text.stroke-47"),sQuery(id+"F44.wireOp",EDGE,"6fba481b-f54a-40dc-850f-529da61e2d5d.sketch_text.stroke-48"),sQuery(id+"F44.wireOp",EDGE,"6fba481b-f54a-40dc-850f-529da61e2d5d.sketch_text.stroke-49")])],"isStart":false})]});}
            extrude(context, id + "F46", {"entities" : qUnion([Q0]), "endBound" : BoundingType.UP_TO_SURFACE, "depth" : 25 * mm, "endBoundEntityFace" : qUnion([Q1]), "offsetDistance" : 25 * mm});
        }
        {
            var Q0;
            Q0=makeQuery(id+"F44.imprint","IMPRINT",FACE,{"disambiguationData":[TD([[makeQuery(id+"F44.imprint","IMPRINT",EDGE,{"derivedFrom":sQuery(id+"F44.wireOp",EDGE,"E202.bottom")}),-1.0]])]});
            var Q1;
            {var subQ0=sQuery(id+"F0.wireOp",EDGE,"E0.right");var subQ1=sQuery(id+"F0.wireOp",EDGE,"E0.bottom");var subQ2=sQuery(id+"F0.wireOp",EDGE,"E1");var subQ4=sQuery(id+"F0.wireOp",EDGE,"E0.left");Q1=makeQuery(id+"F45.boolean.opBoolean","MERGE",FACE,{"derivedFrom":[makeQuery(id+"F6.boolean.opBoolean","SPLIT",FACE,{"disambiguationData":[TD([makeQuery(id+"F1.opExtrude","CAP_FACE",FACE,{"disambiguationData":[OSD([subQ1,sQuery(id+"F0.wireOp",EDGE,"E0.top"),subQ4,subQ0,subQ2])],"isStart":false})])],"derivedFrom":makeQuery(id+"F1.opExtrude","SWEPT_FACE",FACE,{"disambiguationData":[OSD([subQ2])]})}),makeQuery(id+"F45.opExtrude","CAP_FACE",FACE,{"disambiguationData":[OSD([sQuery(id+"F44.wireOp",EDGE,"E200.bottom"),sQuery(id+"F44.wireOp",EDGE,"E200.top"),sQuery(id+"F44.wireOp",EDGE,"E200.left"),sQuery(id+"F44.wireOp",EDGE,"E200.right"),sQuery(id+"F44.wireOp",EDGE,"E201.bottom"),sQuery(id+"F44.wireOp",EDGE,"E201.top"),sQuery(id+"F44.wireOp",EDGE,"E201.left"),sQuery(id+"F44.wireOp",EDGE,"E201.right"),sQuery(id+"F44.wireOp",EDGE,"E202.bottom"),sQuery(id+"F44.wireOp",EDGE,"E202.top"),sQuery(id+"F44.wireOp",EDGE,"E202.left"),sQuery(id+"F44.wireOp",EDGE,"E202.right"),sQuery(id+"F44.wireOp",EDGE,"0e071c30-8112-48db-a0b7-94a150164aee.sketch_text.stroke-0"),sQuery(id+"F44.wireOp",EDGE,"0e071c30-8112-48db-a0b7-94a150164aee.sketch_text.stroke-1"),sQuery(id+"F44.wireOp",EDGE,"0e071c30-8112-48db-a0b7-94a150164aee.sketch_text.stroke-2"),sQuery(id+"F44.wireOp",EDGE,"0e071c30-8112-48db-a0b7-94a150164aee.sketch_text.stroke-3"),sQuery(id+"F44.wireOp",EDGE,"0e071c30-8112-48db-a0b7-94a150164aee.sketch_text.stroke-4"),sQuery(id+"F44.wireOp",EDGE,"0e071c30-8112-48db-a0b7-94a150164aee.sketch_text.stroke-5"),sQuery(id+"F44.wireOp",EDGE,"0e071c30-8112-48db-a0b7-94a150164aee.sketch_text.stroke-6"),sQuery(id+"F44.wireOp",EDGE,"0e071c30-8112-48db-a0b7-94a150164aee.sketch_text.stroke-7"),sQuery(id+"F44.wireOp",EDGE,"0e071c30-8112-48db-a0b7-94a150164aee.sketch_text.stroke-8"),sQuery(id+"F44.wireOp",EDGE,"0e071c30-8112-48db-a0b7-94a150164aee.sketch_text.stroke-9"),sQuery(id+"F44.wireOp",EDGE,"0e071c30-8112-48db-a0b7-94a150164aee.sketch_text.stroke-10"),sQuery(id+"F44.wireOp",EDGE,"0e071c30-8112-48db-a0b7-94a150164aee.sketch_text.stroke-11"),sQuery(id+"F44.wireOp",EDGE,"0e071c30-8112-48db-a0b7-94a150164aee.sketch_text.stroke-12"),sQuery(id+"F44.wireOp",EDGE,"0e071c30-8112-48db-a0b7-94a150164aee.sketch_text.stroke-13"),sQuery(id+"F44.wireOp",EDGE,"0e071c30-8112-48db-a0b7-94a150164aee.sketch_text.stroke-14"),sQuery(id+"F44.wireOp",EDGE,"0e071c30-8112-48db-a0b7-94a150164aee.sketch_text.stroke-15"),sQuery(id+"F44.wireOp",EDGE,"0e071c30-8112-48db-a0b7-94a150164aee.sketch_text.stroke-16"),sQuery(id+"F44.wireOp",EDGE,"0e071c30-8112-48db-a0b7-94a150164aee.sketch_text.stroke-17"),sQuery(id+"F44.wireOp",EDGE,"0e071c30-8112-48db-a0b7-94a150164aee.sketch_text.stroke-18"),sQuery(id+"F44.wireOp",EDGE,"0e071c30-8112-48db-a0b7-94a150164aee.sketch_text.stroke-19"),sQuery(id+"F44.wireOp",EDGE,"0e071c30-8112-48db-a0b7-94a150164aee.sketch_text.stroke-28"),sQuery(id+"F44.wireOp",EDGE,"0e071c30-8112-48db-a0b7-94a150164aee.sketch_text.stroke-29"),sQuery(id+"F44.wireOp",EDGE,"0e071c30-8112-48db-a0b7-94a150164aee.sketch_text.stroke-30"),sQuery(id+"F44.wireOp",EDGE,"0e071c30-8112-48db-a0b7-94a150164aee.sketch_text.stroke-31"),sQuery(id+"F44.wireOp",EDGE,"0e071c30-8112-48db-a0b7-94a150164aee.sketch_text.stroke-32"),sQuery(id+"F44.wireOp",EDGE,"0e071c30-8112-48db-a0b7-94a150164aee.sketch_text.stroke-33"),sQuery(id+"F44.wireOp",EDGE,"0e071c30-8112-48db-a0b7-94a150164aee.sketch_text.stroke-34"),sQuery(id+"F44.wireOp",EDGE,"0e071c30-8112-48db-a0b7-94a150164aee.sketch_text.stroke-35"),sQuery(id+"F44.wireOp",EDGE,"e2d7af9a-f6d1-4b82-89d6-a8a0b8d7c55a.sketch_text.stroke-0"),sQuery(id+"F44.wireOp",EDGE,"e2d7af9a-f6d1-4b82-89d6-a8a0b8d7c55a.sketch_text.stroke-1"),sQuery(id+"F44.wireOp",EDGE,"e2d7af9a-f6d1-4b82-89d6-a8a0b8d7c55a.sketch_text.stroke-2"),sQuery(id+"F44.wireOp",EDGE,"e2d7af9a-f6d1-4b82-89d6-a8a0b8d7c55a.sketch_text.stroke-3"),sQuery(id+"F44.wireOp",EDGE,"e2d7af9a-f6d1-4b82-89d6-a8a0b8d7c55a.sketch_text.stroke-4"),sQuery(id+"F44.wireOp",EDGE,"e2d7af9a-f6d1-4b82-89d6-a8a0b8d7c55a.sketch_text.stroke-5"),sQuery(id+"F44.wireOp",EDGE,"e2d7af9a-f6d1-4b82-89d6-a8a0b8d7c55a.sketch_text.stroke-6"),sQuery(id+"F44.wireOp",EDGE,"e2d7af9a-f6d1-4b82-89d6-a8a0b8d7c55a.sketch_text.stroke-7"),sQuery(id+"F44.wireOp",EDGE,"e2d7af9a-f6d1-4b82-89d6-a8a0b8d7c55a.sketch_text.stroke-8"),sQuery(id+"F44.wireOp",EDGE,"e2d7af9a-f6d1-4b82-89d6-a8a0b8d7c55a.sketch_text.stroke-9"),sQuery(id+"F44.wireOp",EDGE,"e2d7af9a-f6d1-4b82-89d6-a8a0b8d7c55a.sketch_text.stroke-10"),sQuery(id+"F44.wireOp",EDGE,"e2d7af9a-f6d1-4b82-89d6-a8a0b8d7c55a.sketch_text.stroke-11"),sQuery(id+"F44.wireOp",EDGE,"e2d7af9a-f6d1-4b82-89d6-a8a0b8d7c55a.sketch_text.stroke-12"),sQuery(id+"F44.wireOp",EDGE,"e2d7af9a-f6d1-4b82-89d6-a8a0b8d7c55a.sketch_text.stroke-13"),sQuery(id+"F44.wireOp",EDGE,"e2d7af9a-f6d1-4b82-89d6-a8a0b8d7c55a.sketch_text.stroke-14"),sQuery(id+"F44.wireOp",EDGE,"e2d7af9a-f6d1-4b82-89d6-a8a0b8d7c55a.sketch_text.stroke-15"),sQuery(id+"F44.wireOp",EDGE,"e2d7af9a-f6d1-4b82-89d6-a8a0b8d7c55a.sketch_text.stroke-16"),sQuery(id+"F44.wireOp",EDGE,"e2d7af9a-f6d1-4b82-89d6-a8a0b8d7c55a.sketch_text.stroke-17"),sQuery(id+"F44.wireOp",EDGE,"e2d7af9a-f6d1-4b82-89d6-a8a0b8d7c55a.sketch_text.stroke-18"),sQuery(id+"F44.wireOp",EDGE,"e2d7af9a-f6d1-4b82-89d6-a8a0b8d7c55a.sketch_text.stroke-19"),sQuery(id+"F44.wireOp",EDGE,"e2d7af9a-f6d1-4b82-89d6-a8a0b8d7c55a.sketch_text.stroke-20"),sQuery(id+"F44.wireOp",EDGE,"e2d7af9a-f6d1-4b82-89d6-a8a0b8d7c55a.sketch_text.stroke-21"),sQuery(id+"F44.wireOp",EDGE,"e2d7af9a-f6d1-4b82-89d6-a8a0b8d7c55a.sketch_text.stroke-22"),sQuery(id+"F44.wireOp",EDGE,"e2d7af9a-f6d1-4b82-89d6-a8a0b8d7c55a.sketch_text.stroke-31"),sQuery(id+"F44.wireOp",EDGE,"e2d7af9a-f6d1-4b82-89d6-a8a0b8d7c55a.sketch_text.stroke-32"),sQuery(id+"F44.wireOp",EDGE,"e2d7af9a-f6d1-4b82-89d6-a8a0b8d7c55a.sketch_text.stroke-33"),sQuery(id+"F44.wireOp",EDGE,"e2d7af9a-f6d1-4b82-89d6-a8a0b8d7c55a.sketch_text.stroke-34"),sQuery(id+"F44.wireOp",EDGE,"e2d7af9a-f6d1-4b82-89d6-a8a0b8d7c55a.sketch_text.stroke-35"),sQuery(id+"F44.wireOp",EDGE,"e2d7af9a-f6d1-4b82-89d6-a8a0b8d7c55a.sketch_text.stroke-36"),sQuery(id+"F44.wireOp",EDGE,"e2d7af9a-f6d1-4b82-89d6-a8a0b8d7c55a.sketch_text.stroke-37"),sQuery(id+"F44.wireOp",EDGE,"e2d7af9a-f6d1-4b82-89d6-a8a0b8d7c55a.sketch_text.stroke-38"),sQuery(id+"F44.wireOp",EDGE,"e2d7af9a-f6d1-4b82-89d6-a8a0b8d7c55a.sketch_text.stroke-39"),sQuery(id+"F44.wireOp",EDGE,"e2d7af9a-f6d1-4b82-89d6-a8a0b8d7c55a.sketch_text.stroke-40"),sQuery(id+"F44.wireOp",EDGE,"e2d7af9a-f6d1-4b82-89d6-a8a0b8d7c55a.sketch_text.stroke-41"),sQuery(id+"F44.wireOp",EDGE,"e2d7af9a-f6d1-4b82-89d6-a8a0b8d7c55a.sketch_text.stroke-42"),sQuery(id+"F44.wireOp",EDGE,"e2d7af9a-f6d1-4b82-89d6-a8a0b8d7c55a.sketch_text.stroke-43"),sQuery(id+"F44.wireOp",EDGE,"6fba481b-f54a-40dc-850f-529da61e2d5d.sketch_text.stroke-0"),sQuery(id+"F44.wireOp",EDGE,"6fba481b-f54a-40dc-850f-529da61e2d5d.sketch_text.stroke-1"),sQuery(id+"F44.wireOp",EDGE,"6fba481b-f54a-40dc-850f-529da61e2d5d.sketch_text.stroke-2"),sQuery(id+"F44.wireOp",EDGE,"6fba481b-f54a-40dc-850f-529da61e2d5d.sketch_text.stroke-3"),sQuery(id+"F44.wireOp",EDGE,"6fba481b-f54a-40dc-850f-529da61e2d5d.sketch_text.stroke-4"),sQuery(id+"F44.wireOp",EDGE,"6fba481b-f54a-40dc-850f-529da61e2d5d.sketch_text.stroke-5"),sQuery(id+"F44.wireOp",EDGE,"6fba481b-f54a-40dc-850f-529da61e2d5d.sketch_text.stroke-6"),sQuery(id+"F44.wireOp",EDGE,"6fba481b-f54a-40dc-850f-529da61e2d5d.sketch_text.stroke-7"),sQuery(id+"F44.wireOp",EDGE,"6fba481b-f54a-40dc-850f-529da61e2d5d.sketch_text.stroke-8"),sQuery(id+"F44.wireOp",EDGE,"6fba481b-f54a-40dc-850f-529da61e2d5d.sketch_text.stroke-9"),sQuery(id+"F44.wireOp",EDGE,"6fba481b-f54a-40dc-850f-529da61e2d5d.sketch_text.stroke-10"),sQuery(id+"F44.wireOp",EDGE,"6fba481b-f54a-40dc-850f-529da61e2d5d.sketch_text.stroke-11"),sQuery(id+"F44.wireOp",EDGE,"6fba481b-f54a-40dc-850f-529da61e2d5d.sketch_text.stroke-12"),sQuery(id+"F44.wireOp",EDGE,"6fba481b-f54a-40dc-850f-529da61e2d5d.sketch_text.stroke-13"),sQuery(id+"F44.wireOp",EDGE,"6fba481b-f54a-40dc-850f-529da61e2d5d.sketch_text.stroke-22"),sQuery(id+"F44.wireOp",EDGE,"6fba481b-f54a-40dc-850f-529da61e2d5d.sketch_text.stroke-23"),sQuery(id+"F44.wireOp",EDGE,"6fba481b-f54a-40dc-850f-529da61e2d5d.sketch_text.stroke-24"),sQuery(id+"F44.wireOp",EDGE,"6fba481b-f54a-40dc-850f-529da61e2d5d.sketch_text.stroke-25"),sQuery(id+"F44.wireOp",EDGE,"6fba481b-f54a-40dc-850f-529da61e2d5d.sketch_text.stroke-26"),sQuery(id+"F44.wireOp",EDGE,"6fba481b-f54a-40dc-850f-529da61e2d5d.sketch_text.stroke-27"),sQuery(id+"F44.wireOp",EDGE,"6fba481b-f54a-40dc-850f-529da61e2d5d.sketch_text.stroke-28"),sQuery(id+"F44.wireOp",EDGE,"6fba481b-f54a-40dc-850f-529da61e2d5d.sketch_text.stroke-29"),sQuery(id+"F44.wireOp",EDGE,"6fba481b-f54a-40dc-850f-529da61e2d5d.sketch_text.stroke-30"),sQuery(id+"F44.wireOp",EDGE,"6fba481b-f54a-40dc-850f-529da61e2d5d.sketch_text.stroke-31"),sQuery(id+"F44.wireOp",EDGE,"6fba481b-f54a-40dc-850f-529da61e2d5d.sketch_text.stroke-32"),sQuery(id+"F44.wireOp",EDGE,"6fba481b-f54a-40dc-850f-529da61e2d5d.sketch_text.stroke-33"),sQuery(id+"F44.wireOp",EDGE,"6fba481b-f54a-40dc-850f-529da61e2d5d.sketch_text.stroke-34"),sQuery(id+"F44.wireOp",EDGE,"6fba481b-f54a-40dc-850f-529da61e2d5d.sketch_text.stroke-35"),sQuery(id+"F44.wireOp",EDGE,"6fba481b-f54a-40dc-850f-529da61e2d5d.sketch_text.stroke-36"),sQuery(id+"F44.wireOp",EDGE,"6fba481b-f54a-40dc-850f-529da61e2d5d.sketch_text.stroke-37"),sQuery(id+"F44.wireOp",EDGE,"6fba481b-f54a-40dc-850f-529da61e2d5d.sketch_text.stroke-38"),sQuery(id+"F44.wireOp",EDGE,"6fba481b-f54a-40dc-850f-529da61e2d5d.sketch_text.stroke-39"),sQuery(id+"F44.wireOp",EDGE,"6fba481b-f54a-40dc-850f-529da61e2d5d.sketch_text.stroke-40"),sQuery(id+"F44.wireOp",EDGE,"6fba481b-f54a-40dc-850f-529da61e2d5d.sketch_text.stroke-41"),sQuery(id+"F44.wireOp",EDGE,"6fba481b-f54a-40dc-850f-529da61e2d5d.sketch_text.stroke-42"),sQuery(id+"F44.wireOp",EDGE,"6fba481b-f54a-40dc-850f-529da61e2d5d.sketch_text.stroke-43"),sQuery(id+"F44.wireOp",EDGE,"6fba481b-f54a-40dc-850f-529da61e2d5d.sketch_text.stroke-44"),sQuery(id+"F44.wireOp",EDGE,"6fba481b-f54a-40dc-850f-529da61e2d5d.sketch_text.stroke-45"),sQuery(id+"F44.wireOp",EDGE,"6fba481b-f54a-40dc-850f-529da61e2d5d.sketch_text.stroke-46"),sQuery(id+"F44.wireOp",EDGE,"6fba481b-f54a-40dc-850f-529da61e2d5d.sketch_text.stroke-47"),sQuery(id+"F44.wireOp",EDGE,"6fba481b-f54a-40dc-850f-529da61e2d5d.sketch_text.stroke-48"),sQuery(id+"F44.wireOp",EDGE,"6fba481b-f54a-40dc-850f-529da61e2d5d.sketch_text.stroke-49")])],"isStart":false})]});}
            extrude(context, id + "F47", {"entities" : qUnion([Q0]), "endBound" : BoundingType.UP_TO_SURFACE, "depth" : 25 * mm, "endBoundEntityFace" : qUnion([Q1]), "offsetDistance" : 25 * mm});
        }
    });
